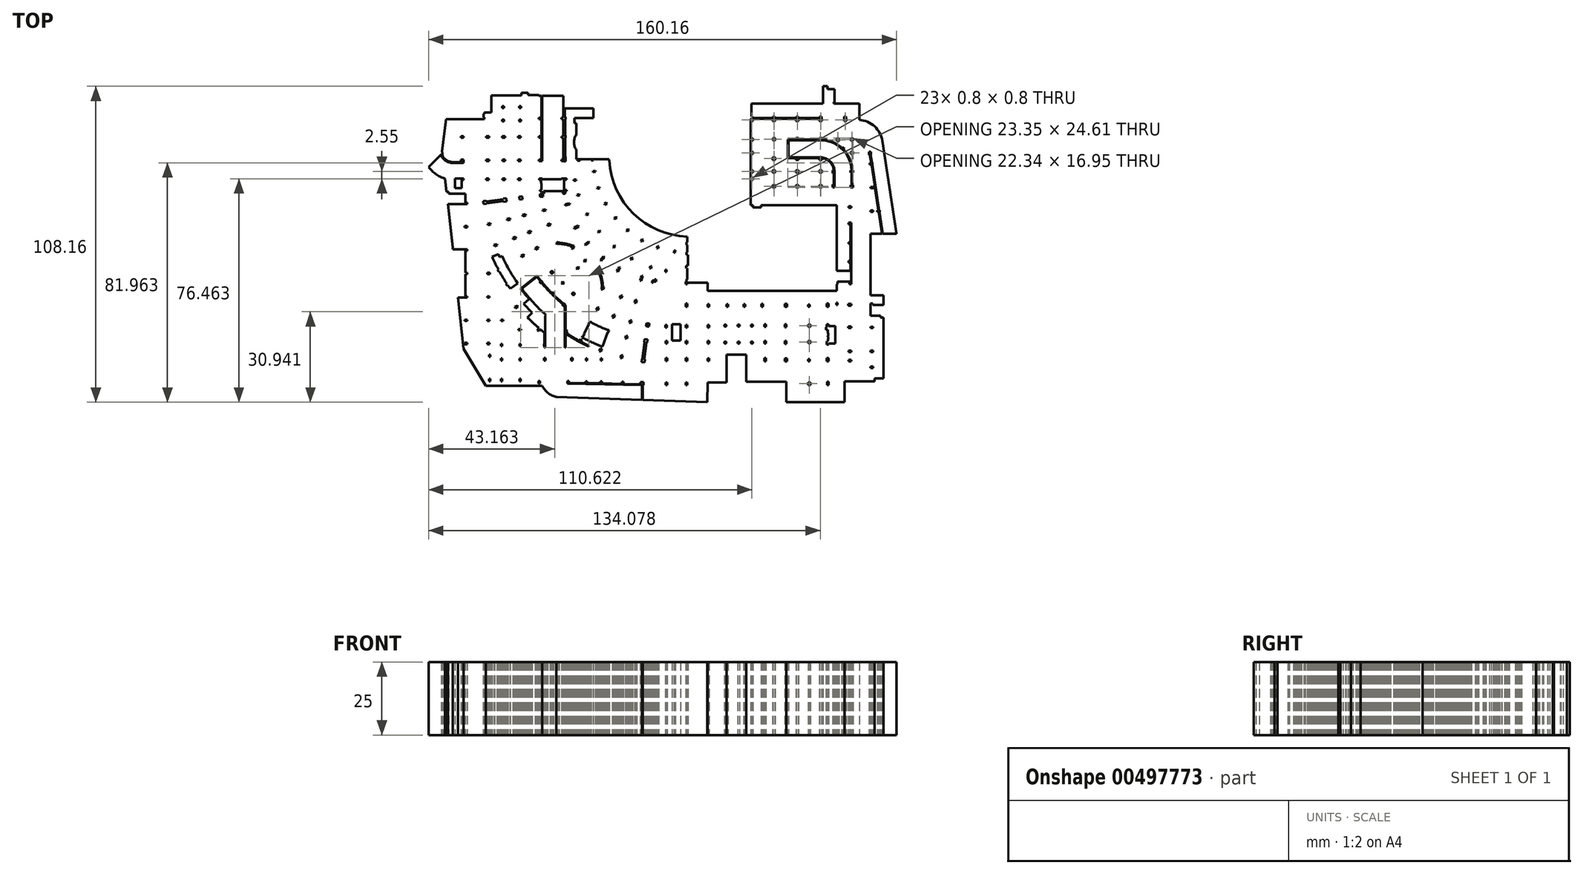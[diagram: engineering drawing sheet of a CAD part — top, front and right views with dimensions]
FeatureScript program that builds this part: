
annotation { "Feature Type Name" : "Feature", "Feature Type Description" : "" }
export const myFeature = defineFeature(function(context is Context, id is Id, definition is map)
    precondition{}
    {
        {
            var Q0;
            Q0=qCreatedBy(makeId("Top.planeOp"),FACE);
            var sketch = newSketch(context, id + "F0", { "sketchPlane" : qUnion([Q0])});
            skLineSegment(sketch, "E0", {"start": v(3.19, -27.44) * mm, "end": v(3.19, -32.96) * mm});
            skLineSegment(sketch, "E1", {"start": v(3.19, -32.96) * mm, "end": v(6.18, -32.96) * mm});
            skLineSegment(sketch, "E2", {"start": v(6.18, -32.96) * mm, "end": v(6.18, -27.44) * mm});
            skLineSegment(sketch, "E3", {"start": v(6.18, -27.44) * mm, "end": v(3.19, -27.44) * mm});
            skLineSegment(sketch, "E4", {"start": v(-41.22, -48.44) * mm, "end": v(-60.5, -48.44) * mm});
            skLineSegment(sketch, "E5", {"start": v(-60.5, -48.44) * mm, "end": v(-68.1, -35.79) * mm});
            skLineSegment(sketch, "E6", {"start": v(-68.1, -35.79) * mm, "end": v(-70, -18.32) * mm});
            skLineSegment(sketch, "E7", {"start": v(-70, -18.32) * mm, "end": v(-66.9, -18.32) * mm});
            skLineSegment(sketch, "E8", {"start": v(-66.9, -18.32) * mm, "end": v(-66.9, -17.92) * mm});
            skLineSegment(sketch, "E9", {"start": v(-66.9, -17.92) * mm, "end": v(-67.46, -17.92) * mm});
            skLineSegment(sketch, "E10", {"start": v(-67.46, -17.92) * mm, "end": v(-67.46, -10.3) * mm});
            skLineSegment(sketch, "E11", {"start": v(-67.46, -10.3) * mm, "end": v(-66.9, -10.3) * mm});
            skLineSegment(sketch, "E12", {"start": v(-66.9, -10.3) * mm, "end": v(-66.9, -9.8) * mm});
            skLineSegment(sketch, "E13", {"start": v(-66.9, -9.8) * mm, "end": v(-67.46, -9.8) * mm});
            skLineSegment(sketch, "E14", {"start": v(-67.46, -9.8) * mm, "end": v(-67.46, -2.3) * mm});
            skLineSegment(sketch, "E15", {"start": v(-67.46, -2.3) * mm, "end": v(-66.9, -2.3) * mm});
            skLineSegment(sketch, "E16", {"start": v(-66.9, -2.3) * mm, "end": v(-66.9, -1.8) * mm});
            skLineSegment(sketch, "E17", {"start": v(-66.9, -1.8) * mm, "end": v(-71.9, -1.8) * mm});
            skLineSegment(sketch, "E18", {"start": v(-71.9, -1.8) * mm, "end": v(-71.88, -1.17) * mm});
            skLineSegment(sketch, "E19", {"start": v(-71.88, -1.17) * mm, "end": v(-73.5, 13.73) * mm});
            skLineSegment(sketch, "E20", {"start": v(-73.5, 13.73) * mm, "end": v(-66.9, 13.73) * mm});
            skLineSegment(sketch, "E21", {"start": v(-66.9, 13.73) * mm, "end": v(-66.9, 14.23) * mm});
            skLineSegment(sketch, "E22", {"start": v(-66.9, 14.23) * mm, "end": v(-67.56, 14.23) * mm});
            skLineSegment(sketch, "E23", {"start": v(-67.56, 14.23) * mm, "end": v(-67.56, 17.23) * mm});
            skLineSegment(sketch, "E24", {"start": v(-67.56, 17.23) * mm, "end": v(-73.17, 17.23) * mm});
            skLineSegment(sketch, "E25", {"start": v(-73.17, 17.23) * mm, "end": v(-73.17, 17.95) * mm});
            skLineSegment(sketch, "E26", {"start": v(-73.17, 17.95) * mm, "end": v(-73.97, 17.95) * mm});
            skLineSegment(sketch, "E27", {"start": v(-73.97, 17.95) * mm, "end": v(-74.47, 22.49) * mm});
            skLineSegment(sketch, "E28", {"start": v(-71.03, 22.46) * mm, "end": v(-68.18, 22.46) * mm});
            skLineSegment(sketch, "E29", {"start": v(-68.18, 22.46) * mm, "end": v(-68.18, 21.96) * mm});
            skLineSegment(sketch, "E30", {"start": v(-68.18, 21.96) * mm, "end": v(-68.83, 21.96) * mm});
            skLineSegment(sketch, "E31", {"start": v(-68.83, 21.96) * mm, "end": v(-68.83, 19.26) * mm});
            skLineSegment(sketch, "E32", {"start": v(-68.83, 19.26) * mm, "end": v(-71.03, 19.26) * mm});
            skLineSegment(sketch, "E33", {"start": v(-71.03, 19.26) * mm, "end": v(-71.03, 22.46) * mm});
            skArc(sketch, "E34", {"start": v(-80.08, 26.47) * mm, "mid": v(-77.61, 24) * mm, "end": v(-74.47, 22.49) * mm});
            skLineSegment(sketch, "E35", {"start": v(-80.08, 26.47) * mm, "end": v(-76.37, 30.18) * mm});
            skLineSegment(sketch, "E36", {"start": v(-76.37, 30.18) * mm, "end": v(-75.78, 30.77) * mm});
            skLineSegment(sketch, "E37", {"start": v(-75.78, 30.77) * mm, "end": v(-75.7, 30.12) * mm});
            skArc(sketch, "E38", {"start": v(-75.7, 30.12) * mm, "mid": v(-73.92, 28.4) * mm, "end": v(-71.51, 27.78) * mm});
            skLineSegment(sketch, "E39", {"start": v(-71.51, 27.78) * mm, "end": v(-68.18, 27.78) * mm});
            skLineSegment(sketch, "E40", {"start": v(-68.18, 27.78) * mm, "end": v(-68.18, 28.98) * mm});
            skLineSegment(sketch, "E41", {"start": v(-68.18, 28.98) * mm, "end": v(-69.08, 28.98) * mm});
            skLineSegment(sketch, "E42", {"start": v(-69.08, 28.98) * mm, "end": v(-69.08, 28.08) * mm});
            skLineSegment(sketch, "E43", {"start": v(-69.08, 28.08) * mm, "end": v(-71.6, 28.08) * mm});
            skArc(sketch, "E44", {"start": v(-75.3, 30.04) * mm, "mid": v(-73.68, 28.6) * mm, "end": v(-71.6, 28.08) * mm});
            skLineSegment(sketch, "E45", {"start": v(-75.3, 30.04) * mm, "end": v(-75.5, 31.91) * mm});
            skLineSegment(sketch, "E46", {"start": v(-75.5, 31.91) * mm, "end": v(-74.07, 42.76) * mm});
            skLineSegment(sketch, "E47", {"start": v(-74.07, 42.76) * mm, "end": v(-60.98, 42.76) * mm});
            skLineSegment(sketch, "E48", {"start": v(-60.98, 42.76) * mm, "end": v(-60.98, 43.46) * mm});
            skLineSegment(sketch, "E49", {"start": v(-60.98, 43.46) * mm, "end": v(-61.28, 43.46) * mm});
            skLineSegment(sketch, "E50", {"start": v(-61.28, 43.46) * mm, "end": v(-61.28, 44.66) * mm});
            skLineSegment(sketch, "E51", {"start": v(-61.28, 44.66) * mm, "end": v(-60.98, 44.66) * mm});
            skLineSegment(sketch, "E52", {"start": v(-60.98, 44.66) * mm, "end": v(-60.98, 45.1) * mm});
            skLineSegment(sketch, "E53", {"start": v(-60.98, 45.1) * mm, "end": v(-58.66, 45.1) * mm});
            skLineSegment(sketch, "E54", {"start": v(-58.66, 45.1) * mm, "end": v(-58.66, 50.96) * mm});
            skLineSegment(sketch, "E55", {"start": v(-58.66, 50.96) * mm, "end": v(-48.31, 50.98) * mm});
            skLineSegment(sketch, "E56", {"start": v(-48.31, 50.98) * mm, "end": v(-48.31, 51.81) * mm});
            skLineSegment(sketch, "E57", {"start": v(-48.31, 51.81) * mm, "end": v(-46.03, 51.81) * mm});
            skLineSegment(sketch, "E58", {"start": v(-46.03, 51.81) * mm, "end": v(-46.03, 51.03) * mm});
            skLineSegment(sketch, "E59", {"start": v(-46.03, 51.03) * mm, "end": v(-42.33, 51.03) * mm});
            skLineSegment(sketch, "E60", {"start": v(-42.33, 51.03) * mm, "end": v(-42.33, 50.78) * mm});
            skLineSegment(sketch, "E61", {"start": v(-42.33, 50.78) * mm, "end": v(-41.48, 50.78) * mm});
            skLineSegment(sketch, "E62", {"start": v(-41.48, 50.78) * mm, "end": v(-41.48, 43.28) * mm});
            skLineSegment(sketch, "E63", {"start": v(-41.48, 43.28) * mm, "end": v(-42.33, 43.28) * mm});
            skLineSegment(sketch, "E64", {"start": v(-42.33, 43.28) * mm, "end": v(-42.33, 42.78) * mm});
            skLineSegment(sketch, "E65", {"start": v(-42.33, 42.78) * mm, "end": v(-41.48, 42.78) * mm});
            skLineSegment(sketch, "E66", {"start": v(-41.48, 42.78) * mm, "end": v(-41.48, 36.98) * mm});
            skLineSegment(sketch, "E67", {"start": v(-41.48, 36.98) * mm, "end": v(-42.33, 36.98) * mm});
            skLineSegment(sketch, "E68", {"start": v(-42.33, 36.98) * mm, "end": v(-42.33, 36.48) * mm});
            skLineSegment(sketch, "E69", {"start": v(-42.33, 36.48) * mm, "end": v(-41.48, 36.48) * mm});
            skLineSegment(sketch, "E70", {"start": v(-41.48, 36.48) * mm, "end": v(-41.48, 28.98) * mm});
            skLineSegment(sketch, "E71", {"start": v(-41.48, 28.98) * mm, "end": v(-42.33, 28.98) * mm});
            skLineSegment(sketch, "E72", {"start": v(-42.33, 28.98) * mm, "end": v(-42.33, 28.48) * mm});
            skLineSegment(sketch, "E73", {"start": v(-42.33, 28.48) * mm, "end": v(-41.23, 28.48) * mm});
            skLineSegment(sketch, "E74", {"start": v(-41.23, 28.48) * mm, "end": v(-41.23, 28.65) * mm});
            skLineSegment(sketch, "E75", {"start": v(-41.23, 28.65) * mm, "end": v(-41.23, 50.78) * mm});
            skLineSegment(sketch, "E76", {"start": v(-41.23, 50.78) * mm, "end": v(-33.98, 50.78) * mm});
            skLineSegment(sketch, "E77", {"start": v(-33.98, 50.78) * mm, "end": v(-33.98, 43.28) * mm});
            skLineSegment(sketch, "E78", {"start": v(-33.98, 43.28) * mm, "end": v(-34.58, 43.28) * mm});
            skLineSegment(sketch, "E79", {"start": v(-34.58, 43.28) * mm, "end": v(-34.58, 42.78) * mm});
            skLineSegment(sketch, "E80", {"start": v(-34.58, 42.78) * mm, "end": v(-33.98, 42.78) * mm});
            skLineSegment(sketch, "E81", {"start": v(-33.98, 42.78) * mm, "end": v(-33.98, 36.9) * mm});
            skLineSegment(sketch, "E82", {"start": v(-33.98, 36.9) * mm, "end": v(-34.58, 36.9) * mm});
            skLineSegment(sketch, "E83", {"start": v(-34.58, 36.9) * mm, "end": v(-34.58, 36.4) * mm});
            skLineSegment(sketch, "E84", {"start": v(-34.58, 36.4) * mm, "end": v(-33.93, 36.4) * mm});
            skLineSegment(sketch, "E85", {"start": v(-33.93, 36.4) * mm, "end": v(-33.93, 28.98) * mm});
            skLineSegment(sketch, "E86", {"start": v(-33.93, 28.98) * mm, "end": v(-34.58, 28.98) * mm});
            skLineSegment(sketch, "E87", {"start": v(-34.58, 28.98) * mm, "end": v(-34.58, 28.48) * mm});
            skLineSegment(sketch, "E88", {"start": v(-34.58, 28.48) * mm, "end": v(-33.63, 28.48) * mm});
            skLineSegment(sketch, "E89", {"start": v(-33.63, 28.48) * mm, "end": v(-33.63, 28.29) * mm});
            skLineSegment(sketch, "E90", {"start": v(-33.63, 28.29) * mm, "end": v(-33.23, 28.29) * mm});
            skLineSegment(sketch, "E91", {"start": v(-33.23, 28.29) * mm, "end": v(-33.23, 29.94) * mm});
            skLineSegment(sketch, "E92", {"start": v(-33.23, 29.94) * mm, "end": v(-33.38, 29.94) * mm});
            skLineSegment(sketch, "E93", {"start": v(-33.38, 29.94) * mm, "end": v(-33.38, 36.4) * mm});
            skLineSegment(sketch, "E94", {"start": v(-33.38, 36.4) * mm, "end": v(-33.23, 36.4) * mm});
            skLineSegment(sketch, "E95", {"start": v(-33.23, 36.4) * mm, "end": v(-33.23, 37.2) * mm});
            skLineSegment(sketch, "E96", {"start": v(-33.23, 37.2) * mm, "end": v(-33.38, 37.2) * mm});
            skLineSegment(sketch, "E97", {"start": v(-33.38, 37.2) * mm, "end": v(-33.38, 42.78) * mm});
            skLineSegment(sketch, "E98", {"start": v(-33.38, 42.78) * mm, "end": v(-33.23, 42.78) * mm});
            skLineSegment(sketch, "E99", {"start": v(-33.23, 42.78) * mm, "end": v(-33.23, 43.58) * mm});
            skLineSegment(sketch, "E100", {"start": v(-33.23, 43.58) * mm, "end": v(-33.51, 43.58) * mm});
            skLineSegment(sketch, "E101", {"start": v(-33.51, 43.58) * mm, "end": v(-33.51, 46.5) * mm});
            skLineSegment(sketch, "E102", {"start": v(-33.51, 46.5) * mm, "end": v(-23.68, 46.5) * mm});
            skLineSegment(sketch, "E103", {"start": v(-23.68, 46.5) * mm, "end": v(-23.68, 43.2) * mm});
            skLineSegment(sketch, "E104", {"start": v(-23.68, 43.2) * mm, "end": v(-30.13, 43.2) * mm});
            skLineSegment(sketch, "E105", {"start": v(-30.13, 43.2) * mm, "end": v(-30.13, 41.39) * mm});
            skLineSegment(sketch, "E106", {"start": v(-30.13, 41.39) * mm, "end": v(-29.51, 41.39) * mm});
            skLineSegment(sketch, "E107", {"start": v(-29.51, 41.39) * mm, "end": v(-29.51, 37.58) * mm});
            skArc(sketch, "E108", {"start": v(-29.51, 37.58) * mm, "mid": v(-30.33, 34.9) * mm, "end": v(-29.51, 32.24) * mm});
            skLineSegment(sketch, "E109", {"start": v(-29.51, 32.24) * mm, "end": v(-29.51, 29.14) * mm});
            skLineSegment(sketch, "E110", {"start": v(-29.51, 29.14) * mm, "end": v(-18.3, 29.09) * mm});
            skLineSegment(sketch, "E111", {"start": v(-18.3, 29.09) * mm, "end": v(-18.3, 28.69) * mm});
            skLineSegment(sketch, "E112", {"start": v(-18.3, 28.69) * mm, "end": v(-18.26, 28.69) * mm});
            skArc(sketch, "E113", {"start": v(-18.26, 28.69) * mm, "mid": v(-9.97, 10.44) * mm, "end": v(8.48, 2.6) * mm});
            skLineSegment(sketch, "E114", {"start": v(8.48, 2.6) * mm, "end": v(8.48, 0.6) * mm});
            skLineSegment(sketch, "E115", {"start": v(8.48, 0.6) * mm, "end": v(8.2, 0.6) * mm});
            skLineSegment(sketch, "E116", {"start": v(8.2, 0.6) * mm, "end": v(8.2, -0.2) * mm});
            skLineSegment(sketch, "E117", {"start": v(8.2, -0.2) * mm, "end": v(8.48, -0.2) * mm});
            skLineSegment(sketch, "E118", {"start": v(8.48, -0.2) * mm, "end": v(8.48, -2.82) * mm});
            skLineSegment(sketch, "E119", {"start": v(8.48, -2.82) * mm, "end": v(8.2, -2.82) * mm});
            skLineSegment(sketch, "E120", {"start": v(8.2, -2.82) * mm, "end": v(8.2, -3.62) * mm});
            skLineSegment(sketch, "E121", {"start": v(8.2, -3.62) * mm, "end": v(8.65, -3.62) * mm});
            skLineSegment(sketch, "E122", {"start": v(8.65, -3.62) * mm, "end": v(8.65, -7.32) * mm});
            skLineSegment(sketch, "E123", {"start": v(8.65, -7.32) * mm, "end": v(8.1, -7.32) * mm});
            skLineSegment(sketch, "E124", {"start": v(8.1, -7.32) * mm, "end": v(8.1, -8.22) * mm});
            skLineSegment(sketch, "E125", {"start": v(8.1, -8.22) * mm, "end": v(8.48, -8.22) * mm});
            skLineSegment(sketch, "E126", {"start": v(8.48, -8.22) * mm, "end": v(8.48, -12) * mm});
            skLineSegment(sketch, "E127", {"start": v(8.48, -12) * mm, "end": v(8.2, -12) * mm});
            skLineSegment(sketch, "E128", {"start": v(8.2, -12) * mm, "end": v(8.2, -12.84) * mm});
            skLineSegment(sketch, "E129", {"start": v(8.2, -12.84) * mm, "end": v(7.96, -12.84) * mm});
            skLineSegment(sketch, "E130", {"start": v(7.96, -12.84) * mm, "end": v(7.96, -13.74) * mm});
            skLineSegment(sketch, "E131", {"start": v(7.96, -13.74) * mm, "end": v(8.46, -13.74) * mm});
            skLineSegment(sketch, "E132", {"start": v(8.46, -13.74) * mm, "end": v(8.46, -13.14) * mm});
            skLineSegment(sketch, "E133", {"start": v(8.46, -13.14) * mm, "end": v(15.42, -13.14) * mm});
            skLineSegment(sketch, "E134", {"start": v(15.42, -13.14) * mm, "end": v(15.42, -15.94) * mm});
            skLineSegment(sketch, "E135", {"start": v(15.42, -15.94) * mm, "end": v(59.59, -15.94) * mm});
            skLineSegment(sketch, "E136", {"start": v(59.59, -15.94) * mm, "end": v(59.59, -13.64) * mm});
            skLineSegment(sketch, "E137", {"start": v(59.59, -13.64) * mm, "end": v(59.87, -13.64) * mm});
            skLineSegment(sketch, "E138", {"start": v(59.87, -13.64) * mm, "end": v(59.87, -12.8) * mm});
            skLineSegment(sketch, "E139", {"start": v(59.87, -12.8) * mm, "end": v(64.62, -12.8) * mm});
            skLineSegment(sketch, "E140", {"start": v(64.62, -12.8) * mm, "end": v(64.62, 7.4) * mm});
            skLineSegment(sketch, "E141", {"start": v(64.62, 7.4) * mm, "end": v(63.62, 7.4) * mm});
            skLineSegment(sketch, "E142", {"start": v(63.62, 7.4) * mm, "end": v(63.62, 6.8) * mm});
            skLineSegment(sketch, "E143", {"start": v(63.62, 6.8) * mm, "end": v(64.37, 6.8) * mm});
            skLineSegment(sketch, "E144", {"start": v(64.37, 6.8) * mm, "end": v(64.37, 0.7) * mm});
            skLineSegment(sketch, "E145", {"start": v(64.37, 0.7) * mm, "end": v(63.62, 0.7) * mm});
            skLineSegment(sketch, "E146", {"start": v(63.62, 0.7) * mm, "end": v(63.62, 0.1) * mm});
            skLineSegment(sketch, "E147", {"start": v(63.62, 0.1) * mm, "end": v(64.37, 0.1) * mm});
            skLineSegment(sketch, "E148", {"start": v(64.37, 0.1) * mm, "end": v(64.37, -5.7) * mm});
            skLineSegment(sketch, "E149", {"start": v(64.37, -5.7) * mm, "end": v(63.62, -5.7) * mm});
            skLineSegment(sketch, "E150", {"start": v(63.62, -5.7) * mm, "end": v(63.62, -6.3) * mm});
            skLineSegment(sketch, "E151", {"start": v(63.62, -6.3) * mm, "end": v(64.37, -6.3) * mm});
            skLineSegment(sketch, "E152", {"start": v(64.37, -6.3) * mm, "end": v(64.37, -9.08) * mm});
            skLineSegment(sketch, "E153", {"start": v(64.37, -9.08) * mm, "end": v(59.59, -9.08) * mm});
            skLineSegment(sketch, "E154", {"start": v(59.59, -9.08) * mm, "end": v(59.59, 13.32) * mm});
            skLineSegment(sketch, "E155", {"start": v(59.59, 13.32) * mm, "end": v(33.72, 13.33) * mm});
            skLineSegment(sketch, "E156", {"start": v(33.72, 13.33) * mm, "end": v(33.72, 12.65) * mm});
            skLineSegment(sketch, "E157", {"start": v(33.72, 12.65) * mm, "end": v(30.94, 12.65) * mm});
            skLineSegment(sketch, "E158", {"start": v(30.94, 12.65) * mm, "end": v(30.94, 13.33) * mm});
            skLineSegment(sketch, "E159", {"start": v(30.94, 13.33) * mm, "end": v(30.1, 13.33) * mm});
            skLineSegment(sketch, "E160", {"start": v(30.1, 13.33) * mm, "end": v(30.1, 43) * mm});
            skLineSegment(sketch, "E161", {"start": v(30.1, 43) * mm, "end": v(54.44, 43) * mm});
            skLineSegment(sketch, "E162", {"start": v(54.44, 43) * mm, "end": v(54.44, 43.7) * mm});
            skLineSegment(sketch, "E163", {"start": v(54.44, 43.7) * mm, "end": v(53.74, 43.7) * mm});
            skLineSegment(sketch, "E164", {"start": v(53.74, 43.7) * mm, "end": v(53.74, 43.26) * mm});
            skLineSegment(sketch, "E165", {"start": v(53.74, 43.26) * mm, "end": v(46.44, 43.26) * mm});
            skLineSegment(sketch, "E166", {"start": v(46.44, 43.26) * mm, "end": v(46.44, 43.7) * mm});
            skLineSegment(sketch, "E167", {"start": v(46.44, 43.7) * mm, "end": v(45.74, 43.7) * mm});
            skLineSegment(sketch, "E168", {"start": v(45.74, 43.7) * mm, "end": v(45.74, 43.26) * mm});
            skLineSegment(sketch, "E169", {"start": v(45.74, 43.26) * mm, "end": v(38.44, 43.26) * mm});
            skLineSegment(sketch, "E170", {"start": v(38.44, 43.26) * mm, "end": v(38.44, 43.7) * mm});
            skLineSegment(sketch, "E171", {"start": v(38.44, 43.7) * mm, "end": v(37.74, 43.7) * mm});
            skLineSegment(sketch, "E172", {"start": v(37.74, 43.7) * mm, "end": v(37.74, 43.26) * mm});
            skLineSegment(sketch, "E173", {"start": v(37.74, 43.26) * mm, "end": v(30.84, 43.26) * mm});
            skLineSegment(sketch, "E174", {"start": v(30.84, 43.26) * mm, "end": v(30.84, 43.7) * mm});
            skLineSegment(sketch, "E175", {"start": v(30.84, 43.7) * mm, "end": v(30.4, 43.7) * mm});
            skLineSegment(sketch, "E176", {"start": v(30.4, 43.7) * mm, "end": v(30.4, 48.19) * mm});
            skLineSegment(sketch, "E177", {"start": v(30.4, 48.19) * mm, "end": v(54.9, 48.19) * mm});
            skLineSegment(sketch, "E178", {"start": v(54.9, 48.19) * mm, "end": v(54.9, 54.08) * mm});
            skLineSegment(sketch, "E179", {"start": v(54.9, 54.08) * mm, "end": v(56.5, 54.08) * mm});
            skLineSegment(sketch, "E180", {"start": v(56.5, 54.08) * mm, "end": v(56.5, 53.08) * mm});
            skLineSegment(sketch, "E181", {"start": v(56.5, 53.08) * mm, "end": v(58.8, 53.08) * mm});
            skLineSegment(sketch, "E182", {"start": v(58.8, 53.08) * mm, "end": v(58.8, 48.68) * mm});
            skLineSegment(sketch, "E183", {"start": v(58.8, 48.68) * mm, "end": v(58.6, 48.68) * mm});
            skLineSegment(sketch, "E184", {"start": v(58.6, 48.68) * mm, "end": v(58.6, 48.18) * mm});
            skLineSegment(sketch, "E185", {"start": v(58.6, 48.18) * mm, "end": v(67.35, 48.18) * mm});
            skLineSegment(sketch, "E186", {"start": v(67.35, 48.18) * mm, "end": v(67.37, 48.18) * mm});
            skLineSegment(sketch, "E187", {"start": v(67.37, 48.18) * mm, "end": v(67.37, 42.54) * mm});
            skArc(sketch, "E188", {"start": v(75.2, 35.39) * mm, "mid": v(72.55, 40.35) * mm, "end": v(67.37, 42.54) * mm});
            skLineSegment(sketch, "E189", {"start": v(75.2, 35.39) * mm, "end": v(80.08, 3.6) * mm});
            skLineSegment(sketch, "E190", {"start": v(80.08, 3.6) * mm, "end": v(75.37, 3.6) * mm});
            skLineSegment(sketch, "E191", {"start": v(75.37, 3.6) * mm, "end": v(74.22, 11.1) * mm});
            skLineSegment(sketch, "E192", {"start": v(74.22, 11.1) * mm, "end": v(74.33, 11.1) * mm});
            skLineSegment(sketch, "E193", {"start": v(74.33, 11.1) * mm, "end": v(74.33, 11.6) * mm});
            skLineSegment(sketch, "E194", {"start": v(74.33, 11.6) * mm, "end": v(74.15, 11.6) * mm});
            skLineSegment(sketch, "E195", {"start": v(74.15, 11.6) * mm, "end": v(71.75, 27.2) * mm});
            skLineSegment(sketch, "E196", {"start": v(71.75, 27.2) * mm, "end": v(71.86, 27.2) * mm});
            skLineSegment(sketch, "E197", {"start": v(71.86, 27.2) * mm, "end": v(71.86, 27.8) * mm});
            skLineSegment(sketch, "E198", {"start": v(71.86, 27.8) * mm, "end": v(71.66, 27.8) * mm});
            skLineSegment(sketch, "E199", {"start": v(71.66, 27.8) * mm, "end": v(71.22, 30.68) * mm});
            skLineSegment(sketch, "E200", {"start": v(71.22, 30.68) * mm, "end": v(71.3, 30.68) * mm});
            skLineSegment(sketch, "E201", {"start": v(71.3, 30.68) * mm, "end": v(71.3, 31.68) * mm});
            skLineSegment(sketch, "E202", {"start": v(71.3, 31.68) * mm, "end": v(70.7, 31.68) * mm});
            skLineSegment(sketch, "E203", {"start": v(70.7, 31.68) * mm, "end": v(70.7, 30.68) * mm});
            skLineSegment(sketch, "E204", {"start": v(70.7, 30.68) * mm, "end": v(70.97, 30.68) * mm});
            skLineSegment(sketch, "E205", {"start": v(70.97, 30.68) * mm, "end": v(71.4, 27.8) * mm});
            skLineSegment(sketch, "E206", {"start": v(71.4, 27.8) * mm, "end": v(70.86, 27.8) * mm});
            skLineSegment(sketch, "E207", {"start": v(70.86, 27.8) * mm, "end": v(70.86, 27.2) * mm});
            skLineSegment(sketch, "E208", {"start": v(70.86, 27.2) * mm, "end": v(71.5, 27.2) * mm});
            skLineSegment(sketch, "E209", {"start": v(71.5, 27.2) * mm, "end": v(72.67, 19.6) * mm});
            skLineSegment(sketch, "E210", {"start": v(72.67, 19.6) * mm, "end": v(71.17, 19.6) * mm});
            skLineSegment(sketch, "E211", {"start": v(71.17, 19.6) * mm, "end": v(71.17, 19.2) * mm});
            skLineSegment(sketch, "E212", {"start": v(71.17, 19.2) * mm, "end": v(72.73, 19.2) * mm});
            skLineSegment(sketch, "E213", {"start": v(72.73, 19.2) * mm, "end": v(73.9, 11.6) * mm});
            skLineSegment(sketch, "E214", {"start": v(73.9, 11.6) * mm, "end": v(73.43, 11.6) * mm});
            skLineSegment(sketch, "E215", {"start": v(73.43, 11.6) * mm, "end": v(73.43, 11.1) * mm});
            skLineSegment(sketch, "E216", {"start": v(73.43, 11.1) * mm, "end": v(73.97, 11.1) * mm});
            skLineSegment(sketch, "E217", {"start": v(73.97, 11.1) * mm, "end": v(75.12, 3.6) * mm});
            skLineSegment(sketch, "E218", {"start": v(75.12, 3.6) * mm, "end": v(71.17, 3.6) * mm});
            skLineSegment(sketch, "E219", {"start": v(71.17, 3.6) * mm, "end": v(71.17, -17.5) * mm});
            skLineSegment(sketch, "E220", {"start": v(71.17, -17.5) * mm, "end": v(75.66, -17.5) * mm});
            skLineSegment(sketch, "E221", {"start": v(75.66, -17.5) * mm, "end": v(75.66, -20.8) * mm});
            skLineSegment(sketch, "E222", {"start": v(75.66, -20.8) * mm, "end": v(71.97, -20.8) * mm});
            skLineSegment(sketch, "E223", {"start": v(71.97, -20.8) * mm, "end": v(71.97, -20.24) * mm});
            skLineSegment(sketch, "E224", {"start": v(71.97, -20.24) * mm, "end": v(71.17, -20.24) * mm});
            skLineSegment(sketch, "E225", {"start": v(71.17, -20.24) * mm, "end": v(71.17, -24.46) * mm});
            skLineSegment(sketch, "E226", {"start": v(71.17, -24.46) * mm, "end": v(74.64, -24.46) * mm});
            skLineSegment(sketch, "E227", {"start": v(74.64, -24.46) * mm, "end": v(74.64, -25.18) * mm});
            skLineSegment(sketch, "E228", {"start": v(74.64, -25.18) * mm, "end": v(75.66, -25.18) * mm});
            skLineSegment(sketch, "E229", {"start": v(75.66, -25.18) * mm, "end": v(75.66, -46) * mm});
            skLineSegment(sketch, "E230", {"start": v(75.66, -46) * mm, "end": v(72.54, -46) * mm});
            skLineSegment(sketch, "E231", {"start": v(72.54, -46) * mm, "end": v(72.54, -47.02) * mm});
            skLineSegment(sketch, "E232", {"start": v(72.54, -47.02) * mm, "end": v(62.34, -47.02) * mm});
            skLineSegment(sketch, "E233", {"start": v(62.34, -47.02) * mm, "end": v(62.34, -54.08) * mm});
            skLineSegment(sketch, "E234", {"start": v(62.34, -54.08) * mm, "end": v(42.34, -54.08) * mm});
            skLineSegment(sketch, "E235", {"start": v(42.34, -54.08) * mm, "end": v(42.34, -47.1) * mm});
            skLineSegment(sketch, "E236", {"start": v(42.34, -47.1) * mm, "end": v(28.57, -47.1) * mm});
            skLineSegment(sketch, "E237", {"start": v(28.57, -47.1) * mm, "end": v(28.57, -37.77) * mm});
            skLineSegment(sketch, "E238", {"start": v(28.57, -37.77) * mm, "end": v(21.87, -37.77) * mm});
            skLineSegment(sketch, "E239", {"start": v(21.87, -37.77) * mm, "end": v(21.87, -47.3) * mm});
            skLineSegment(sketch, "E240", {"start": v(21.87, -47.3) * mm, "end": v(15.42, -47.3) * mm});
            skLineSegment(sketch, "E241", {"start": v(15.42, -47.3) * mm, "end": v(15.23, -54.08) * mm});
            skLineSegment(sketch, "E242", {"start": v(15.23, -54.08) * mm, "end": v(-6.8, -53.3) * mm});
            skLineSegment(sketch, "E243", {"start": v(-6.8, -53.3) * mm, "end": v(-6.8, -48.2) * mm});
            skLineSegment(sketch, "E244", {"start": v(-6.8, -48.2) * mm, "end": v(-6.56, -48.2) * mm});
            skLineSegment(sketch, "E245", {"start": v(-6.56, -48.2) * mm, "end": v(-6.56, -47.2) * mm});
            skLineSegment(sketch, "E246", {"start": v(-6.56, -47.2) * mm, "end": v(-7.6, -47.2) * mm});
            skLineSegment(sketch, "E247", {"start": v(-7.6, -47.2) * mm, "end": v(-7.6, -47.93) * mm});
            skLineSegment(sketch, "E248", {"start": v(-7.6, -47.93) * mm, "end": v(-13.46, -47.81) * mm});
            skLineSegment(sketch, "E249", {"start": v(-13.46, -47.81) * mm, "end": v(-13.46, -47.16) * mm});
            skLineSegment(sketch, "E250", {"start": v(-13.46, -47.16) * mm, "end": v(-13.96, -47.16) * mm});
            skLineSegment(sketch, "E251", {"start": v(-13.96, -47.16) * mm, "end": v(-13.96, -47.8) * mm});
            skLineSegment(sketch, "E252", {"start": v(-13.96, -47.8) * mm, "end": v(-20.76, -47.67) * mm});
            skLineSegment(sketch, "E253", {"start": v(-20.76, -47.67) * mm, "end": v(-20.76, -47.01) * mm});
            skLineSegment(sketch, "E254", {"start": v(-20.76, -47.01) * mm, "end": v(-21.26, -47.01) * mm});
            skLineSegment(sketch, "E255", {"start": v(-21.26, -47.01) * mm, "end": v(-21.26, -47.66) * mm});
            skLineSegment(sketch, "E256", {"start": v(-21.26, -47.66) * mm, "end": v(-25.8, -47.57) * mm});
            skLineSegment(sketch, "E257", {"start": v(-25.8, -47.57) * mm, "end": v(-25.8, -46.92) * mm});
            skLineSegment(sketch, "E258", {"start": v(-25.8, -46.92) * mm, "end": v(-26.3, -46.92) * mm});
            skLineSegment(sketch, "E259", {"start": v(-26.3, -46.92) * mm, "end": v(-26.3, -47.56) * mm});
            skLineSegment(sketch, "E260", {"start": v(-26.3, -47.56) * mm, "end": v(-32.08, -47.44) * mm});
            skLineSegment(sketch, "E261", {"start": v(-32.08, -47.44) * mm, "end": v(-32.08, -46.8) * mm});
            skLineSegment(sketch, "E262", {"start": v(-32.08, -46.8) * mm, "end": v(-32.58, -46.8) * mm});
            skLineSegment(sketch, "E263", {"start": v(-32.58, -46.8) * mm, "end": v(-32.58, -47.7) * mm});
            skLineSegment(sketch, "E264", {"start": v(-32.58, -47.7) * mm, "end": v(-7.06, -48.2) * mm});
            skLineSegment(sketch, "E265", {"start": v(-7.06, -48.2) * mm, "end": v(-7.06, -53.29) * mm});
            skLineSegment(sketch, "E266", {"start": v(-7.06, -53.29) * mm, "end": v(-36.42, -52.25) * mm});
            skArc(sketch, "E267", {"start": v(-41.22, -48.44) * mm, "mid": v(-39.28, -50.93) * mm, "end": v(-36.42, -52.25) * mm});
            skLineSegment(sketch, "E268", {"start": v(-54.88, 36.48) * mm, "end": v(-54.88, 36.98) * mm});
            skLineSegment(sketch, "E269", {"start": v(-54.88, 36.98) * mm, "end": v(-53.98, 36.98) * mm});
            skLineSegment(sketch, "E270", {"start": v(-53.98, 36.98) * mm, "end": v(-53.98, 36.48) * mm});
            skLineSegment(sketch, "E271", {"start": v(-53.98, 36.48) * mm, "end": v(-54.88, 36.48) * mm});
            skLineSegment(sketch, "E272", {"start": v(-69.08, 36.98) * mm, "end": v(-69.08, 36.48) * mm});
            skLineSegment(sketch, "E273", {"start": v(-69.08, 36.48) * mm, "end": v(-68.18, 36.48) * mm});
            skLineSegment(sketch, "E274", {"start": v(-68.18, 36.48) * mm, "end": v(-68.18, 36.98) * mm});
            skLineSegment(sketch, "E275", {"start": v(-68.18, 36.98) * mm, "end": v(-69.08, 36.98) * mm});
            skLineSegment(sketch, "E276", {"start": v(-54.88, 47.2) * mm, "end": v(-54.88, 46.6) * mm});
            skLineSegment(sketch, "E277", {"start": v(-54.88, 46.6) * mm, "end": v(-54.28, 46.6) * mm});
            skLineSegment(sketch, "E278", {"start": v(-54.28, 46.6) * mm, "end": v(-54.28, 47.2) * mm});
            skLineSegment(sketch, "E279", {"start": v(-54.28, 47.2) * mm, "end": v(-54.88, 47.2) * mm});
            skLineSegment(sketch, "E280", {"start": v(-49.08, 47.2) * mm, "end": v(-49.08, 46.6) * mm});
            skLineSegment(sketch, "E281", {"start": v(-49.08, 46.6) * mm, "end": v(-48.48, 46.6) * mm});
            skLineSegment(sketch, "E282", {"start": v(-48.48, 46.6) * mm, "end": v(-48.48, 47.2) * mm});
            skLineSegment(sketch, "E283", {"start": v(-48.48, 47.2) * mm, "end": v(-49.08, 47.2) * mm});
            skCircle(sketch, "E284", {"center": v(-54.58, 42.35) * mm, "radius": 0.35 * mm});
            skCircle(sketch, "E285", {"center": v(-48.78, 42.35) * mm, "radius": 0.35 * mm});
            skLineSegment(sketch, "E286", {"start": v(-60.43, 36.98) * mm, "end": v(-60.43, 36.48) * mm});
            skLineSegment(sketch, "E287", {"start": v(-60.43, 36.48) * mm, "end": v(-59.43, 36.48) * mm});
            skLineSegment(sketch, "E288", {"start": v(-59.43, 36.48) * mm, "end": v(-59.43, 36.98) * mm});
            skLineSegment(sketch, "E289", {"start": v(-59.43, 36.98) * mm, "end": v(-60.43, 36.98) * mm});
            skLineSegment(sketch, "E290", {"start": v(-49.43, 36.98) * mm, "end": v(-49.43, 36.48) * mm});
            skLineSegment(sketch, "E291", {"start": v(-49.43, 36.48) * mm, "end": v(-48.53, 36.48) * mm});
            skLineSegment(sketch, "E292", {"start": v(-48.53, 36.48) * mm, "end": v(-48.53, 36.98) * mm});
            skLineSegment(sketch, "E293", {"start": v(-48.53, 36.98) * mm, "end": v(-49.43, 36.98) * mm});
            skLineSegment(sketch, "E294", {"start": v(-60.43, 28.98) * mm, "end": v(-60.43, 28.48) * mm});
            skLineSegment(sketch, "E295", {"start": v(-60.43, 28.48) * mm, "end": v(-59.33, 28.48) * mm});
            skLineSegment(sketch, "E296", {"start": v(-59.33, 28.48) * mm, "end": v(-59.33, 28.98) * mm});
            skLineSegment(sketch, "E297", {"start": v(-59.33, 28.98) * mm, "end": v(-60.43, 28.98) * mm});
            skLineSegment(sketch, "E298", {"start": v(-54.83, 28.98) * mm, "end": v(-54.83, 28.48) * mm});
            skLineSegment(sketch, "E299", {"start": v(-54.83, 28.48) * mm, "end": v(-53.93, 28.48) * mm});
            skLineSegment(sketch, "E300", {"start": v(-53.93, 28.48) * mm, "end": v(-53.93, 28.98) * mm});
            skLineSegment(sketch, "E301", {"start": v(-53.93, 28.98) * mm, "end": v(-54.83, 28.98) * mm});
            skLineSegment(sketch, "E302", {"start": v(-49.43, 28.48) * mm, "end": v(-49.43, 28.98) * mm});
            skLineSegment(sketch, "E303", {"start": v(-49.43, 28.98) * mm, "end": v(-48.53, 28.98) * mm});
            skLineSegment(sketch, "E304", {"start": v(-48.53, 28.98) * mm, "end": v(-48.53, 28.48) * mm});
            skLineSegment(sketch, "E305", {"start": v(-48.53, 28.48) * mm, "end": v(-49.43, 28.48) * mm});
            skLineSegment(sketch, "E306", {"start": v(-60.43, 22.46) * mm, "end": v(-60.43, 21.96) * mm});
            skLineSegment(sketch, "E307", {"start": v(-60.43, 21.96) * mm, "end": v(-59.53, 21.96) * mm});
            skLineSegment(sketch, "E308", {"start": v(-59.53, 21.96) * mm, "end": v(-59.53, 22.46) * mm});
            skLineSegment(sketch, "E309", {"start": v(-59.53, 22.46) * mm, "end": v(-60.43, 22.46) * mm});
            skLineSegment(sketch, "E310", {"start": v(-54.83, 22.46) * mm, "end": v(-54.83, 21.96) * mm});
            skLineSegment(sketch, "E311", {"start": v(-54.83, 21.96) * mm, "end": v(-53.93, 21.96) * mm});
            skLineSegment(sketch, "E312", {"start": v(-53.93, 21.96) * mm, "end": v(-53.93, 22.46) * mm});
            skLineSegment(sketch, "E313", {"start": v(-53.93, 22.46) * mm, "end": v(-54.83, 22.46) * mm});
            skLineSegment(sketch, "E314", {"start": v(-49.43, 22.46) * mm, "end": v(-49.43, 21.96) * mm});
            skLineSegment(sketch, "E315", {"start": v(-49.43, 21.96) * mm, "end": v(-48.53, 21.96) * mm});
            skLineSegment(sketch, "E316", {"start": v(-48.53, 21.96) * mm, "end": v(-48.53, 22.46) * mm});
            skLineSegment(sketch, "E317", {"start": v(-48.53, 22.46) * mm, "end": v(-49.43, 22.46) * mm});
            skLineSegment(sketch, "E318", {"start": v(-61.37, 14.72) * mm, "end": v(-60.37, 14.85) * mm});
            skLineSegment(sketch, "E319", {"start": v(-60.37, 14.85) * mm, "end": v(-60.35, 14.65) * mm});
            skLineSegment(sketch, "E320", {"start": v(-60.35, 14.65) * mm, "end": v(-54.53, 15.4) * mm});
            skLineSegment(sketch, "E321", {"start": v(-54.53, 15.4) * mm, "end": v(-54.55, 15.6) * mm});
            skLineSegment(sketch, "E322", {"start": v(-54.55, 15.6) * mm, "end": v(-53.56, 15.72) * mm});
            skLineSegment(sketch, "E323", {"start": v(-53.56, 15.72) * mm, "end": v(-53.43, 14.68) * mm});
            skLineSegment(sketch, "E324", {"start": v(-53.43, 14.68) * mm, "end": v(-54.42, 14.55) * mm});
            skLineSegment(sketch, "E325", {"start": v(-54.42, 14.55) * mm, "end": v(-54.44, 14.75) * mm});
            skLineSegment(sketch, "E326", {"start": v(-54.44, 14.75) * mm, "end": v(-60.27, 14) * mm});
            skLineSegment(sketch, "E327", {"start": v(-60.27, 14) * mm, "end": v(-60.24, 13.8) * mm});
            skLineSegment(sketch, "E328", {"start": v(-60.24, 13.8) * mm, "end": v(-61.23, 13.68) * mm});
            skLineSegment(sketch, "E329", {"start": v(-61.23, 13.68) * mm, "end": v(-61.37, 14.72) * mm});
            skLineSegment(sketch, "E330", {"start": v(-49.09, 16.3) * mm, "end": v(-48.96, 15.25) * mm});
            skLineSegment(sketch, "E331", {"start": v(-48.96, 15.25) * mm, "end": v(-47.96, 15.38) * mm});
            skLineSegment(sketch, "E332", {"start": v(-47.96, 15.38) * mm, "end": v(-48.1, 16.42) * mm});
            skLineSegment(sketch, "E333", {"start": v(-48.1, 16.42) * mm, "end": v(-49.09, 16.3) * mm});
            skLineSegment(sketch, "E334", {"start": v(-59.94, 6.97) * mm, "end": v(-58.97, 7.22) * mm});
            skLineSegment(sketch, "E335", {"start": v(-58.97, 7.22) * mm, "end": v(-58.85, 6.73) * mm});
            skLineSegment(sketch, "E336", {"start": v(-58.85, 6.73) * mm, "end": v(-59.82, 6.49) * mm});
            skLineSegment(sketch, "E337", {"start": v(-59.82, 6.49) * mm, "end": v(-59.94, 6.97) * mm});
            skLineSegment(sketch, "E338", {"start": v(-53.28, 8.66) * mm, "end": v(-53.16, 8.18) * mm});
            skLineSegment(sketch, "E339", {"start": v(-53.16, 8.18) * mm, "end": v(-52.19, 8.42) * mm});
            skLineSegment(sketch, "E340", {"start": v(-52.19, 8.42) * mm, "end": v(-52.3, 8.9) * mm});
            skLineSegment(sketch, "E341", {"start": v(-52.3, 8.9) * mm, "end": v(-53.28, 8.66) * mm});
            skLineSegment(sketch, "E342", {"start": v(-47.95, 10) * mm, "end": v(-46.98, 10.25) * mm});
            skLineSegment(sketch, "E343", {"start": v(-46.98, 10.25) * mm, "end": v(-46.85, 9.77) * mm});
            skLineSegment(sketch, "E344", {"start": v(-46.85, 9.77) * mm, "end": v(-47.82, 9.52) * mm});
            skLineSegment(sketch, "E345", {"start": v(-47.82, 9.52) * mm, "end": v(-47.95, 10) * mm});
            skLineSegment(sketch, "E346", {"start": v(-67.8, 6.2) * mm, "end": v(-66.9, 6.2) * mm});
            skLineSegment(sketch, "E347", {"start": v(-66.9, 6.2) * mm, "end": v(-66.9, 5.7) * mm});
            skLineSegment(sketch, "E348", {"start": v(-66.9, 5.7) * mm, "end": v(-67.8, 5.7) * mm});
            skLineSegment(sketch, "E349", {"start": v(-67.8, 5.7) * mm, "end": v(-67.8, 6.2) * mm});
            skLineSegment(sketch, "E350", {"start": v(-57.67, -0.28) * mm, "end": v(-56.73, 0.08) * mm});
            skLineSegment(sketch, "E351", {"start": v(-56.73, 0.08) * mm, "end": v(-56.55, -0.39) * mm});
            skLineSegment(sketch, "E352", {"start": v(-56.55, -0.39) * mm, "end": v(-57.49, -0.75) * mm});
            skLineSegment(sketch, "E353", {"start": v(-57.49, -0.75) * mm, "end": v(-57.67, -0.28) * mm});
            skLineSegment(sketch, "E354", {"start": v(-51.25, 2.2) * mm, "end": v(-50.32, 2.56) * mm});
            skLineSegment(sketch, "E355", {"start": v(-50.32, 2.56) * mm, "end": v(-50.14, 2.09) * mm});
            skLineSegment(sketch, "E356", {"start": v(-50.14, 2.09) * mm, "end": v(-51.07, 1.73) * mm});
            skLineSegment(sketch, "E357", {"start": v(-51.07, 1.73) * mm, "end": v(-51.25, 2.2) * mm});
            skLineSegment(sketch, "E358", {"start": v(-46.12, 4.18) * mm, "end": v(-45.19, 4.54) * mm});
            skLineSegment(sketch, "E359", {"start": v(-45.19, 4.54) * mm, "end": v(-45, 4.07) * mm});
            skLineSegment(sketch, "E360", {"start": v(-45, 4.07) * mm, "end": v(-45.94, 3.7) * mm});
            skLineSegment(sketch, "E361", {"start": v(-45.94, 3.7) * mm, "end": v(-46.12, 4.18) * mm});
            skLineSegment(sketch, "E362", {"start": v(-48.47, -3.98) * mm, "end": v(-47.58, -3.5) * mm});
            skLineSegment(sketch, "E363", {"start": v(-47.58, -3.5) * mm, "end": v(-47.35, -3.95) * mm});
            skLineSegment(sketch, "E364", {"start": v(-47.35, -3.95) * mm, "end": v(-48.23, -4.42) * mm});
            skLineSegment(sketch, "E365", {"start": v(-48.23, -4.42) * mm, "end": v(-48.47, -3.98) * mm});
            skLineSegment(sketch, "E366", {"start": v(-43.61, -1.4) * mm, "end": v(-42.73, -0.93) * mm});
            skLineSegment(sketch, "E367", {"start": v(-42.73, -0.93) * mm, "end": v(-42.5, -1.37) * mm});
            skLineSegment(sketch, "E368", {"start": v(-42.5, -1.37) * mm, "end": v(-43.38, -1.84) * mm});
            skLineSegment(sketch, "E369", {"start": v(-43.38, -1.84) * mm, "end": v(-43.61, -1.4) * mm});
            skLineSegment(sketch, "E370", {"start": v(-60, -9.8) * mm, "end": v(-59.1, -9.8) * mm});
            skLineSegment(sketch, "E371", {"start": v(-59.1, -9.8) * mm, "end": v(-59.1, -10.3) * mm});
            skLineSegment(sketch, "E372", {"start": v(-59.1, -10.3) * mm, "end": v(-60, -10.3) * mm});
            skLineSegment(sketch, "E373", {"start": v(-60, -10.3) * mm, "end": v(-60, -9.8) * mm});
            skLineSegment(sketch, "E374", {"start": v(-54.98, -4.06) * mm, "end": v(-55.78, -4.43) * mm});
            skLineSegment(sketch, "E375", {"start": v(-55.78, -4.43) * mm, "end": v(-56.27, -3.35) * mm});
            skLineSegment(sketch, "E376", {"start": v(-56.27, -3.35) * mm, "end": v(-58.34, -4.33) * mm});
            skArc(sketch, "E377", {"start": v(-58.34, -4.33) * mm, "mid": v(-57.32, -6.51) * mm, "end": v(-56.23, -8.65) * mm});
            skLineSegment(sketch, "E378", {"start": v(-56.23, -8.65) * mm, "end": v(-56.47, -8.78) * mm});
            skLineSegment(sketch, "E379", {"start": v(-56.47, -8.78) * mm, "end": v(-56.1, -9.48) * mm});
            skLineSegment(sketch, "E380", {"start": v(-56.1, -9.48) * mm, "end": v(-55.85, -9.35) * mm});
            skArc(sketch, "E381", {"start": v(-55.85, -9.35) * mm, "mid": v(-54.67, -11.4) * mm, "end": v(-53.41, -13.4) * mm});
            skLineSegment(sketch, "E382", {"start": v(-53.41, -13.4) * mm, "end": v(-53.65, -13.56) * mm});
            skLineSegment(sketch, "E383", {"start": v(-53.65, -13.56) * mm, "end": v(-53.2, -14.22) * mm});
            skLineSegment(sketch, "E384", {"start": v(-53.2, -14.22) * mm, "end": v(-52.97, -14.07) * mm});
            skLineSegment(sketch, "E385", {"start": v(-52.97, -14.07) * mm, "end": v(-52.87, -14.23) * mm});
            skLineSegment(sketch, "E386", {"start": v(-52.87, -14.23) * mm, "end": v(-52.16, -15.25) * mm});
            skLineSegment(sketch, "E387", {"start": v(-52.16, -15.25) * mm, "end": v(-49.57, -13.42) * mm});
            skLineSegment(sketch, "E388", {"start": v(-49.57, -13.42) * mm, "end": v(-50.27, -12.4) * mm});
            skArc(sketch, "E389", {"start": v(-54.98, -4.06) * mm, "mid": v(-52.79, -8.32) * mm, "end": v(-50.27, -12.4) * mm});
            skLineSegment(sketch, "E390", {"start": v(-50.62, -21.47) * mm, "end": v(-49.71, -21.04) * mm});
            skLineSegment(sketch, "E391", {"start": v(-49.71, -21.04) * mm, "end": v(-49.5, -21.5) * mm});
            skLineSegment(sketch, "E392", {"start": v(-49.5, -21.5) * mm, "end": v(-50.4, -21.92) * mm});
            skLineSegment(sketch, "E393", {"start": v(-50.4, -21.92) * mm, "end": v(-50.62, -21.47) * mm});
            skLineSegment(sketch, "E394", {"start": v(-60, -17.92) * mm, "end": v(-59.2, -17.92) * mm});
            skLineSegment(sketch, "E395", {"start": v(-59.2, -17.92) * mm, "end": v(-59.2, -18.32) * mm});
            skLineSegment(sketch, "E396", {"start": v(-59.2, -18.32) * mm, "end": v(-60, -18.32) * mm});
            skLineSegment(sketch, "E397", {"start": v(-60, -18.32) * mm, "end": v(-60, -17.92) * mm});
            skLineSegment(sketch, "E398", {"start": v(-67.7, -25.87) * mm, "end": v(-66.9, -25.87) * mm});
            skLineSegment(sketch, "E399", {"start": v(-66.9, -25.87) * mm, "end": v(-66.9, -26.27) * mm});
            skLineSegment(sketch, "E400", {"start": v(-66.9, -26.27) * mm, "end": v(-67.7, -26.27) * mm});
            skLineSegment(sketch, "E401", {"start": v(-67.7, -26.27) * mm, "end": v(-67.7, -25.87) * mm});
            skLineSegment(sketch, "E402", {"start": v(-60, -25.87) * mm, "end": v(-60, -26.27) * mm});
            skLineSegment(sketch, "E403", {"start": v(-60, -26.27) * mm, "end": v(-59.2, -26.27) * mm});
            skLineSegment(sketch, "E404", {"start": v(-59.2, -26.27) * mm, "end": v(-59.2, -25.87) * mm});
            skLineSegment(sketch, "E405", {"start": v(-59.2, -25.87) * mm, "end": v(-60, -25.87) * mm});
            skLineSegment(sketch, "E406", {"start": v(-55.36, -25.87) * mm, "end": v(-54.56, -25.87) * mm});
            skLineSegment(sketch, "E407", {"start": v(-54.56, -25.87) * mm, "end": v(-54.56, -26.27) * mm});
            skLineSegment(sketch, "E408", {"start": v(-54.56, -26.27) * mm, "end": v(-55.36, -26.27) * mm});
            skLineSegment(sketch, "E409", {"start": v(-55.36, -26.27) * mm, "end": v(-55.36, -25.87) * mm});
            skLineSegment(sketch, "E410", {"start": v(-67.7, -33.82) * mm, "end": v(-66.9, -33.82) * mm});
            skLineSegment(sketch, "E411", {"start": v(-66.9, -33.82) * mm, "end": v(-66.9, -34.22) * mm});
            skLineSegment(sketch, "E412", {"start": v(-66.9, -34.22) * mm, "end": v(-67.7, -34.22) * mm});
            skLineSegment(sketch, "E413", {"start": v(-67.7, -34.22) * mm, "end": v(-67.7, -33.82) * mm});
            skLineSegment(sketch, "E414", {"start": v(-59.4, -46.92) * mm, "end": v(-59.4, -46.12) * mm});
            skLineSegment(sketch, "E415", {"start": v(-59.4, -46.12) * mm, "end": v(-59, -46.12) * mm});
            skLineSegment(sketch, "E416", {"start": v(-59, -46.12) * mm, "end": v(-59, -46.92) * mm});
            skLineSegment(sketch, "E417", {"start": v(-59, -46.92) * mm, "end": v(-59.4, -46.92) * mm});
            skLineSegment(sketch, "E418", {"start": v(-55.3, -46.92) * mm, "end": v(-55.3, -46.12) * mm});
            skLineSegment(sketch, "E419", {"start": v(-55.3, -46.12) * mm, "end": v(-54.9, -46.12) * mm});
            skLineSegment(sketch, "E420", {"start": v(-54.9, -46.12) * mm, "end": v(-54.9, -46.92) * mm});
            skLineSegment(sketch, "E421", {"start": v(-54.9, -46.92) * mm, "end": v(-55.3, -46.92) * mm});
            skLineSegment(sketch, "E422", {"start": v(-60, -34.22) * mm, "end": v(-60, -33.82) * mm});
            skLineSegment(sketch, "E423", {"start": v(-60, -33.82) * mm, "end": v(-59.2, -33.82) * mm});
            skLineSegment(sketch, "E424", {"start": v(-59.2, -33.82) * mm, "end": v(-59.2, -34.22) * mm});
            skLineSegment(sketch, "E425", {"start": v(-59.2, -34.22) * mm, "end": v(-60, -34.22) * mm});
            skLineSegment(sketch, "E426", {"start": v(-55.3, -34.92) * mm, "end": v(-55.3, -34.12) * mm});
            skLineSegment(sketch, "E427", {"start": v(-55.3, -34.12) * mm, "end": v(-54.9, -34.12) * mm});
            skLineSegment(sketch, "E428", {"start": v(-54.9, -34.12) * mm, "end": v(-54.9, -34.92) * mm});
            skLineSegment(sketch, "E429", {"start": v(-54.9, -34.92) * mm, "end": v(-55.3, -34.92) * mm});
            skLineSegment(sketch, "E430", {"start": v(-59.4, -38.62) * mm, "end": v(-59.4, -37.82) * mm});
            skLineSegment(sketch, "E431", {"start": v(-59.4, -37.82) * mm, "end": v(-59, -37.82) * mm});
            skLineSegment(sketch, "E432", {"start": v(-59, -37.82) * mm, "end": v(-59, -38.62) * mm});
            skLineSegment(sketch, "E433", {"start": v(-59, -38.62) * mm, "end": v(-59.4, -38.62) * mm});
            skLineSegment(sketch, "E434", {"start": v(-55.3, -39.92) * mm, "end": v(-55.3, -39.12) * mm});
            skLineSegment(sketch, "E435", {"start": v(-55.3, -39.12) * mm, "end": v(-54.9, -39.12) * mm});
            skLineSegment(sketch, "E436", {"start": v(-54.9, -39.12) * mm, "end": v(-54.9, -39.92) * mm});
            skLineSegment(sketch, "E437", {"start": v(-54.9, -39.92) * mm, "end": v(-55.3, -39.92) * mm});
            skLineSegment(sketch, "E438", {"start": v(-49, -46.92) * mm, "end": v(-49, -46.12) * mm});
            skLineSegment(sketch, "E439", {"start": v(-49, -46.12) * mm, "end": v(-48.6, -46.12) * mm});
            skLineSegment(sketch, "E440", {"start": v(-48.6, -46.12) * mm, "end": v(-48.6, -46.92) * mm});
            skLineSegment(sketch, "E441", {"start": v(-48.6, -46.92) * mm, "end": v(-49, -46.92) * mm});
            skLineSegment(sketch, "E442", {"start": v(-49, -39.92) * mm, "end": v(-49, -39.12) * mm});
            skLineSegment(sketch, "E443", {"start": v(-49, -39.12) * mm, "end": v(-48.6, -39.12) * mm});
            skLineSegment(sketch, "E444", {"start": v(-48.6, -39.12) * mm, "end": v(-48.6, -39.92) * mm});
            skLineSegment(sketch, "E445", {"start": v(-48.6, -39.92) * mm, "end": v(-49, -39.92) * mm});
            skLineSegment(sketch, "E446", {"start": v(-49, -34.92) * mm, "end": v(-49, -34.12) * mm});
            skLineSegment(sketch, "E447", {"start": v(-49, -34.12) * mm, "end": v(-48.6, -34.12) * mm});
            skLineSegment(sketch, "E448", {"start": v(-48.6, -34.12) * mm, "end": v(-48.6, -34.92) * mm});
            skLineSegment(sketch, "E449", {"start": v(-48.6, -34.92) * mm, "end": v(-49, -34.92) * mm});
            skLineSegment(sketch, "E450", {"start": v(-49.3, -29.02) * mm, "end": v(-49.3, -29.42) * mm});
            skLineSegment(sketch, "E451", {"start": v(-49.3, -29.42) * mm, "end": v(-48.5, -29.42) * mm});
            skLineSegment(sketch, "E452", {"start": v(-48.5, -29.42) * mm, "end": v(-48.5, -29.02) * mm});
            skLineSegment(sketch, "E453", {"start": v(-48.5, -29.02) * mm, "end": v(-49.3, -29.02) * mm});
            skLineSegment(sketch, "E454", {"start": v(-40.61, -39.02) * mm, "end": v(-40.61, -39.92) * mm});
            skLineSegment(sketch, "E455", {"start": v(-40.61, -39.92) * mm, "end": v(-40.11, -39.92) * mm});
            skLineSegment(sketch, "E456", {"start": v(-40.11, -39.92) * mm, "end": v(-40.11, -39.02) * mm});
            skLineSegment(sketch, "E457", {"start": v(-40.11, -39.02) * mm, "end": v(-40.61, -39.02) * mm});
            skLineSegment(sketch, "E458", {"start": v(-42.48, -47.7) * mm, "end": v(-42.48, -46.8) * mm});
            skLineSegment(sketch, "E459", {"start": v(-42.48, -46.8) * mm, "end": v(-41.98, -46.8) * mm});
            skLineSegment(sketch, "E460", {"start": v(-41.98, -46.8) * mm, "end": v(-41.98, -47.7) * mm});
            skLineSegment(sketch, "E461", {"start": v(-41.98, -47.7) * mm, "end": v(-42.48, -47.7) * mm});
            skLineSegment(sketch, "E462", {"start": v(-40.46, -35.44) * mm, "end": v(-40.21, -35.44) * mm});
            skLineSegment(sketch, "E463", {"start": v(-40.21, -35.44) * mm, "end": v(-40.2, -24.53) * mm});
            skLineSegment(sketch, "E464", {"start": v(-40.2, -24.53) * mm, "end": v(-39.94, -24.24) * mm});
            skArc(sketch, "E465", {"start": v(-48.24, -15.25) * mm, "mid": v(-44.31, -19.95) * mm, "end": v(-39.94, -24.24) * mm});
            skLineSegment(sketch, "E466", {"start": v(-48.24, -15.25) * mm, "end": v(-43.04, -11.19) * mm});
            skLineSegment(sketch, "E467", {"start": v(-43.04, -11.19) * mm, "end": v(-41.87, -12.7) * mm});
            skArc(sketch, "E468", {"start": v(-41.87, -12.7) * mm, "mid": v(-41.9, -13.24) * mm, "end": v(-41.36, -13.3) * mm});
            skArc(sketch, "E469", {"start": v(-41.36, -13.3) * mm, "mid": v(-37.95, -17.06) * mm, "end": v(-34.2, -20.47) * mm});
            skArc(sketch, "E470", {"start": v(-34.2, -20.47) * mm, "mid": v(-34.13, -21.02) * mm, "end": v(-33.58, -20.98) * mm});
            skLineSegment(sketch, "E471", {"start": v(-33.58, -20.98) * mm, "end": v(-33.5, -21.04) * mm});
            skLineSegment(sketch, "E472", {"start": v(-33.5, -21.04) * mm, "end": v(-33.5, -35.44) * mm});
            skLineSegment(sketch, "E473", {"start": v(-33.5, -35.44) * mm, "end": v(-33.26, -35.44) * mm});
            skLineSegment(sketch, "E474", {"start": v(-33.26, -35.44) * mm, "end": v(-33.26, -30.6) * mm});
            skArc(sketch, "E475", {"start": v(-33.26, -30.6) * mm, "mid": v(-29.4, -32.94) * mm, "end": v(-25.37, -35) * mm});
            skLineSegment(sketch, "E476", {"start": v(-25.37, -35) * mm, "end": v(-25.24, -34.73) * mm});
            skArc(sketch, "E477", {"start": v(-27.96, -33.38) * mm, "mid": v(-26.6, -34.07) * mm, "end": v(-25.24, -34.73) * mm});
            skLineSegment(sketch, "E478", {"start": v(-27.96, -33.38) * mm, "end": v(-27.63, -32.76) * mm});
            skLineSegment(sketch, "E479", {"start": v(-27.63, -32.76) * mm, "end": v(-28.07, -32.53) * mm});
            skLineSegment(sketch, "E480", {"start": v(-28.07, -32.53) * mm, "end": v(-28.4, -33.15) * mm});
            skArc(sketch, "E481", {"start": v(-32.92, -30.47) * mm, "mid": v(-30.69, -31.85) * mm, "end": v(-28.4, -33.15) * mm});
            skLineSegment(sketch, "E482", {"start": v(-32.92, -30.47) * mm, "end": v(-32.54, -29.88) * mm});
            skLineSegment(sketch, "E483", {"start": v(-32.54, -29.88) * mm, "end": v(-33.26, -29.41) * mm});
            skLineSegment(sketch, "E484", {"start": v(-33.26, -29.41) * mm, "end": v(-33.26, -20.92) * mm});
            skLineSegment(sketch, "E485", {"start": v(-33.26, -20.92) * mm, "end": v(-33.48, -20.74) * mm});
            skArc(sketch, "E486", {"start": v(-33.48, -20.74) * mm, "mid": v(-33.62, -20.4) * mm, "end": v(-33.99, -20.32) * mm});
            skArc(sketch, "E487", {"start": v(-37.56, -17.09) * mm, "mid": v(-35.8, -18.75) * mm, "end": v(-33.99, -20.32) * mm});
            skLineSegment(sketch, "E488", {"start": v(-37.56, -17.09) * mm, "end": v(-37.31, -16.85) * mm});
            skLineSegment(sketch, "E489", {"start": v(-37.31, -16.85) * mm, "end": v(-37.74, -16.42) * mm});
            skLineSegment(sketch, "E490", {"start": v(-37.74, -16.42) * mm, "end": v(-37.98, -16.67) * mm});
            skArc(sketch, "E491", {"start": v(-41.22, -13.1) * mm, "mid": v(-39.64, -14.92) * mm, "end": v(-37.98, -16.67) * mm});
            skArc(sketch, "E492", {"start": v(-41.22, -13.1) * mm, "mid": v(-41.29, -12.73) * mm, "end": v(-41.63, -12.59) * mm});
            skArc(sketch, "E493", {"start": v(-43, -10.84) * mm, "mid": v(-42.32, -11.72) * mm, "end": v(-41.63, -12.59) * mm});
            skLineSegment(sketch, "E494", {"start": v(-43, -10.84) * mm, "end": v(-48.6, -15.2) * mm});
            skArc(sketch, "E495", {"start": v(-48.6, -15.2) * mm, "mid": v(-47.19, -17) * mm, "end": v(-45.72, -18.76) * mm});
            skLineSegment(sketch, "E496", {"start": v(-45.72, -18.76) * mm, "end": v(-47.6, -20.4) * mm});
            skLineSegment(sketch, "E497", {"start": v(-47.6, -20.4) * mm, "end": v(-44.7, -23.52) * mm});
            skLineSegment(sketch, "E498", {"start": v(-44.7, -23.52) * mm, "end": v(-46.27, -25.1) * mm});
            skLineSegment(sketch, "E499", {"start": v(-42.41, -28.68) * mm, "end": v(-42.8, -29.52) * mm});
            skLineSegment(sketch, "E500", {"start": v(-42.8, -29.52) * mm, "end": v(-42.35, -29.73) * mm});
            skLineSegment(sketch, "E501", {"start": v(-42.35, -29.73) * mm, "end": v(-42.02, -29.02) * mm});
            skLineSegment(sketch, "E502", {"start": v(-42.02, -29.02) * mm, "end": v(-40.46, -30.3) * mm});
            skLineSegment(sketch, "E503", {"start": v(-40.46, -30.3) * mm, "end": v(-40.46, -34.12) * mm});
            skLineSegment(sketch, "E504", {"start": v(-40.46, -34.12) * mm, "end": v(-40.61, -34.12) * mm});
            skLineSegment(sketch, "E505", {"start": v(-40.61, -34.12) * mm, "end": v(-40.61, -34.92) * mm});
            skLineSegment(sketch, "E506", {"start": v(-40.61, -34.92) * mm, "end": v(-40.46, -34.92) * mm});
            skLineSegment(sketch, "E507", {"start": v(-40.46, -34.92) * mm, "end": v(-40.46, -35.44) * mm});
            skArc(sketch, "E508", {"start": v(-46.27, -25.1) * mm, "mid": v(-44.38, -26.93) * mm, "end": v(-42.41, -28.68) * mm});
            skLineSegment(sketch, "E509", {"start": v(-31.36, -39.02) * mm, "end": v(-31.36, -39.92) * mm});
            skLineSegment(sketch, "E510", {"start": v(-31.36, -39.92) * mm, "end": v(-30.86, -39.92) * mm});
            skLineSegment(sketch, "E511", {"start": v(-30.86, -39.92) * mm, "end": v(-30.86, -39.02) * mm});
            skLineSegment(sketch, "E512", {"start": v(-30.86, -39.02) * mm, "end": v(-31.36, -39.02) * mm});
            skLineSegment(sketch, "E513", {"start": v(-26.26, -39.12) * mm, "end": v(-26.26, -39.92) * mm});
            skLineSegment(sketch, "E514", {"start": v(-26.26, -39.92) * mm, "end": v(-25.86, -39.92) * mm});
            skLineSegment(sketch, "E515", {"start": v(-25.86, -39.92) * mm, "end": v(-25.86, -39.12) * mm});
            skLineSegment(sketch, "E516", {"start": v(-25.86, -39.12) * mm, "end": v(-26.26, -39.12) * mm});
            skLineSegment(sketch, "E517", {"start": v(-21.2, -39.12) * mm, "end": v(-21.2, -39.92) * mm});
            skLineSegment(sketch, "E518", {"start": v(-21.2, -39.92) * mm, "end": v(-20.8, -39.92) * mm});
            skLineSegment(sketch, "E519", {"start": v(-20.8, -39.92) * mm, "end": v(-20.8, -39.12) * mm});
            skLineSegment(sketch, "E520", {"start": v(-20.8, -39.12) * mm, "end": v(-21.2, -39.12) * mm});
            skLineSegment(sketch, "E521", {"start": v(1.07, -47.3) * mm, "end": v(1.07, -48.2) * mm});
            skLineSegment(sketch, "E522", {"start": v(1.07, -48.2) * mm, "end": v(1.57, -48.2) * mm});
            skLineSegment(sketch, "E523", {"start": v(1.57, -48.2) * mm, "end": v(1.57, -47.3) * mm});
            skLineSegment(sketch, "E524", {"start": v(1.57, -47.3) * mm, "end": v(1.07, -47.3) * mm});
            skLineSegment(sketch, "E525", {"start": v(7.96, -47.3) * mm, "end": v(7.96, -48.2) * mm});
            skLineSegment(sketch, "E526", {"start": v(7.96, -48.2) * mm, "end": v(8.46, -48.2) * mm});
            skLineSegment(sketch, "E527", {"start": v(8.46, -48.2) * mm, "end": v(8.46, -47.3) * mm});
            skLineSegment(sketch, "E528", {"start": v(8.46, -47.3) * mm, "end": v(7.96, -47.3) * mm});
            skLineSegment(sketch, "E529", {"start": v(15.42, -39.12) * mm, "end": v(15.42, -40.02) * mm});
            skLineSegment(sketch, "E530", {"start": v(15.42, -40.02) * mm, "end": v(15.92, -40.02) * mm});
            skLineSegment(sketch, "E531", {"start": v(15.92, -40.02) * mm, "end": v(15.92, -39.12) * mm});
            skLineSegment(sketch, "E532", {"start": v(15.92, -39.12) * mm, "end": v(15.42, -39.12) * mm});
            skLineSegment(sketch, "E533", {"start": v(7.96, -38.92) * mm, "end": v(7.96, -40.02) * mm});
            skLineSegment(sketch, "E534", {"start": v(7.96, -40.02) * mm, "end": v(8.46, -40.02) * mm});
            skLineSegment(sketch, "E535", {"start": v(8.46, -40.02) * mm, "end": v(8.46, -38.92) * mm});
            skLineSegment(sketch, "E536", {"start": v(8.46, -38.92) * mm, "end": v(7.96, -38.92) * mm});
            skLineSegment(sketch, "E537", {"start": v(7.97, -33.1) * mm, "end": v(7.97, -34) * mm});
            skLineSegment(sketch, "E538", {"start": v(7.97, -34) * mm, "end": v(8.47, -34) * mm});
            skLineSegment(sketch, "E539", {"start": v(8.47, -34) * mm, "end": v(8.47, -33.1) * mm});
            skLineSegment(sketch, "E540", {"start": v(8.47, -33.1) * mm, "end": v(7.97, -33.1) * mm});
            skLineSegment(sketch, "E541", {"start": v(15.42, -33.1) * mm, "end": v(15.42, -34) * mm});
            skLineSegment(sketch, "E542", {"start": v(15.42, -34) * mm, "end": v(15.92, -34) * mm});
            skLineSegment(sketch, "E543", {"start": v(15.92, -34) * mm, "end": v(15.92, -33.1) * mm});
            skLineSegment(sketch, "E544", {"start": v(15.92, -33.1) * mm, "end": v(15.42, -33.1) * mm});
            skLineSegment(sketch, "E545", {"start": v(7.97, -27.64) * mm, "end": v(7.97, -28.54) * mm});
            skLineSegment(sketch, "E546", {"start": v(7.97, -28.54) * mm, "end": v(8.47, -28.54) * mm});
            skLineSegment(sketch, "E547", {"start": v(8.47, -28.54) * mm, "end": v(8.47, -27.64) * mm});
            skLineSegment(sketch, "E548", {"start": v(8.47, -27.64) * mm, "end": v(7.97, -27.64) * mm});
            skLineSegment(sketch, "E549", {"start": v(15.42, -27.64) * mm, "end": v(15.42, -28.54) * mm});
            skLineSegment(sketch, "E550", {"start": v(15.42, -28.54) * mm, "end": v(15.92, -28.54) * mm});
            skLineSegment(sketch, "E551", {"start": v(15.92, -28.54) * mm, "end": v(15.92, -27.64) * mm});
            skLineSegment(sketch, "E552", {"start": v(15.92, -27.64) * mm, "end": v(15.42, -27.64) * mm});
            skLineSegment(sketch, "E553", {"start": v(1.07, -39.02) * mm, "end": v(1.07, -40.02) * mm});
            skLineSegment(sketch, "E554", {"start": v(1.07, -40.02) * mm, "end": v(1.57, -40.02) * mm});
            skLineSegment(sketch, "E555", {"start": v(1.57, -40.02) * mm, "end": v(1.57, -39.02) * mm});
            skLineSegment(sketch, "E556", {"start": v(1.57, -39.02) * mm, "end": v(1.07, -39.02) * mm});
            skLineSegment(sketch, "E557", {"start": v(1.07, -33.1) * mm, "end": v(1.07, -34) * mm});
            skLineSegment(sketch, "E558", {"start": v(1.07, -34) * mm, "end": v(1.57, -34) * mm});
            skLineSegment(sketch, "E559", {"start": v(1.57, -34) * mm, "end": v(1.57, -33.1) * mm});
            skLineSegment(sketch, "E560", {"start": v(1.57, -33.1) * mm, "end": v(1.07, -33.1) * mm});
            skLineSegment(sketch, "E561", {"start": v(0.97, -27.64) * mm, "end": v(0.97, -28.54) * mm});
            skLineSegment(sketch, "E562", {"start": v(0.97, -28.54) * mm, "end": v(1.47, -28.54) * mm});
            skLineSegment(sketch, "E563", {"start": v(1.47, -28.54) * mm, "end": v(1.47, -27.64) * mm});
            skLineSegment(sketch, "E564", {"start": v(1.47, -27.64) * mm, "end": v(0.97, -27.64) * mm});
            skLineSegment(sketch, "E565", {"start": v(7.97, -20.34) * mm, "end": v(7.97, -21.44) * mm});
            skLineSegment(sketch, "E566", {"start": v(7.97, -21.44) * mm, "end": v(8.47, -21.44) * mm});
            skLineSegment(sketch, "E567", {"start": v(8.47, -21.44) * mm, "end": v(8.47, -20.34) * mm});
            skLineSegment(sketch, "E568", {"start": v(8.47, -20.34) * mm, "end": v(7.97, -20.34) * mm});
            skLineSegment(sketch, "E569", {"start": v(15.42, -20.54) * mm, "end": v(15.42, -21.44) * mm});
            skLineSegment(sketch, "E570", {"start": v(15.42, -21.44) * mm, "end": v(15.92, -21.44) * mm});
            skLineSegment(sketch, "E571", {"start": v(15.92, -21.44) * mm, "end": v(15.92, -20.54) * mm});
            skLineSegment(sketch, "E572", {"start": v(15.92, -20.54) * mm, "end": v(15.42, -20.54) * mm});
            skLineSegment(sketch, "E573", {"start": v(21.84, -20.54) * mm, "end": v(21.84, -21.44) * mm});
            skLineSegment(sketch, "E574", {"start": v(21.84, -21.44) * mm, "end": v(22.34, -21.44) * mm});
            skLineSegment(sketch, "E575", {"start": v(22.34, -21.44) * mm, "end": v(22.34, -20.54) * mm});
            skLineSegment(sketch, "E576", {"start": v(22.34, -20.54) * mm, "end": v(21.84, -20.54) * mm});
            skLineSegment(sketch, "E577", {"start": v(27.77, -20.54) * mm, "end": v(27.77, -21.44) * mm});
            skLineSegment(sketch, "E578", {"start": v(27.77, -21.44) * mm, "end": v(28.27, -21.44) * mm});
            skLineSegment(sketch, "E579", {"start": v(28.27, -21.44) * mm, "end": v(28.27, -20.54) * mm});
            skLineSegment(sketch, "E580", {"start": v(28.27, -20.54) * mm, "end": v(27.77, -20.54) * mm});
            skLineSegment(sketch, "E581", {"start": v(33.84, -20.44) * mm, "end": v(33.84, -21.44) * mm});
            skLineSegment(sketch, "E582", {"start": v(33.84, -21.44) * mm, "end": v(34.34, -21.44) * mm});
            skLineSegment(sketch, "E583", {"start": v(34.34, -21.44) * mm, "end": v(34.34, -20.44) * mm});
            skLineSegment(sketch, "E584", {"start": v(34.34, -20.44) * mm, "end": v(33.84, -20.44) * mm});
            skLineSegment(sketch, "E585", {"start": v(41.84, -20.44) * mm, "end": v(41.84, -21.44) * mm});
            skLineSegment(sketch, "E586", {"start": v(41.84, -21.44) * mm, "end": v(42.64, -21.44) * mm});
            skLineSegment(sketch, "E587", {"start": v(42.64, -21.44) * mm, "end": v(42.64, -20.44) * mm});
            skLineSegment(sketch, "E588", {"start": v(42.64, -20.44) * mm, "end": v(41.84, -20.44) * mm});
            skLineSegment(sketch, "E589", {"start": v(49.9, -20.64) * mm, "end": v(49.9, -21.44) * mm});
            skLineSegment(sketch, "E590", {"start": v(49.9, -21.44) * mm, "end": v(50.3, -21.44) * mm});
            skLineSegment(sketch, "E591", {"start": v(50.3, -21.44) * mm, "end": v(50.3, -20.64) * mm});
            skLineSegment(sketch, "E592", {"start": v(50.3, -20.64) * mm, "end": v(49.9, -20.64) * mm});
            skLineSegment(sketch, "E593", {"start": v(56.24, -20.34) * mm, "end": v(56.24, -21.44) * mm});
            skLineSegment(sketch, "E594", {"start": v(56.24, -21.44) * mm, "end": v(56.84, -21.44) * mm});
            skLineSegment(sketch, "E595", {"start": v(56.84, -21.44) * mm, "end": v(56.84, -20.34) * mm});
            skLineSegment(sketch, "E596", {"start": v(56.84, -20.34) * mm, "end": v(56.24, -20.34) * mm});
            skLineSegment(sketch, "E597", {"start": v(59.52, -20.03) * mm, "end": v(59.52, -20.83) * mm});
            skLineSegment(sketch, "E598", {"start": v(59.52, -20.83) * mm, "end": v(59.92, -20.83) * mm});
            skLineSegment(sketch, "E599", {"start": v(59.92, -20.83) * mm, "end": v(59.92, -20.03) * mm});
            skLineSegment(sketch, "E600", {"start": v(59.92, -20.03) * mm, "end": v(59.52, -20.03) * mm});
            skLineSegment(sketch, "E601", {"start": v(63.5, -20.44) * mm, "end": v(63.5, -21.04) * mm});
            skLineSegment(sketch, "E602", {"start": v(63.5, -21.04) * mm, "end": v(64.6, -21.04) * mm});
            skLineSegment(sketch, "E603", {"start": v(64.6, -21.04) * mm, "end": v(64.6, -20.44) * mm});
            skLineSegment(sketch, "E604", {"start": v(64.6, -20.44) * mm, "end": v(63.5, -20.44) * mm});
            skLineSegment(sketch, "E605", {"start": v(63.92, -12.84) * mm, "end": v(63.92, -13.64) * mm});
            skLineSegment(sketch, "E606", {"start": v(63.92, -13.64) * mm, "end": v(64.52, -13.64) * mm});
            skLineSegment(sketch, "E607", {"start": v(64.52, -13.64) * mm, "end": v(64.52, -12.84) * mm});
            skLineSegment(sketch, "E608", {"start": v(64.52, -12.84) * mm, "end": v(63.92, -12.84) * mm});
            skLineSegment(sketch, "E609", {"start": v(63.5, -28.14) * mm, "end": v(63.5, -28.74) * mm});
            skLineSegment(sketch, "E610", {"start": v(63.5, -28.74) * mm, "end": v(64.6, -28.74) * mm});
            skLineSegment(sketch, "E611", {"start": v(64.6, -28.74) * mm, "end": v(64.6, -28.14) * mm});
            skLineSegment(sketch, "E612", {"start": v(64.6, -28.14) * mm, "end": v(63.5, -28.14) * mm});
            skLineSegment(sketch, "E613", {"start": v(71.17, -28.24) * mm, "end": v(71.17, -28.74) * mm});
            skLineSegment(sketch, "E614", {"start": v(71.17, -28.74) * mm, "end": v(72.07, -28.74) * mm});
            skLineSegment(sketch, "E615", {"start": v(72.07, -28.74) * mm, "end": v(72.07, -28.24) * mm});
            skLineSegment(sketch, "E616", {"start": v(72.07, -28.24) * mm, "end": v(71.17, -28.24) * mm});
            skLineSegment(sketch, "E617", {"start": v(71.17, -36.44) * mm, "end": v(71.17, -36.94) * mm});
            skLineSegment(sketch, "E618", {"start": v(71.17, -36.94) * mm, "end": v(72.07, -36.94) * mm});
            skLineSegment(sketch, "E619", {"start": v(72.07, -36.94) * mm, "end": v(72.07, -36.44) * mm});
            skLineSegment(sketch, "E620", {"start": v(72.07, -36.44) * mm, "end": v(71.17, -36.44) * mm});
            skLineSegment(sketch, "E621", {"start": v(63.7, -36.44) * mm, "end": v(63.7, -36.94) * mm});
            skLineSegment(sketch, "E622", {"start": v(63.7, -36.94) * mm, "end": v(64.6, -36.94) * mm});
            skLineSegment(sketch, "E623", {"start": v(64.6, -36.94) * mm, "end": v(64.6, -36.44) * mm});
            skLineSegment(sketch, "E624", {"start": v(64.6, -36.44) * mm, "end": v(63.7, -36.44) * mm});
            skLineSegment(sketch, "E625", {"start": v(63.7, -39.6) * mm, "end": v(63.7, -40.1) * mm});
            skLineSegment(sketch, "E626", {"start": v(63.7, -40.1) * mm, "end": v(64.6, -40.1) * mm});
            skLineSegment(sketch, "E627", {"start": v(64.6, -40.1) * mm, "end": v(64.6, -39.6) * mm});
            skLineSegment(sketch, "E628", {"start": v(64.6, -39.6) * mm, "end": v(63.7, -39.6) * mm});
            skLineSegment(sketch, "E629", {"start": v(71.17, -42.44) * mm, "end": v(71.17, -41.94) * mm});
            skLineSegment(sketch, "E630", {"start": v(71.17, -41.94) * mm, "end": v(72.07, -41.94) * mm});
            skLineSegment(sketch, "E631", {"start": v(72.07, -41.94) * mm, "end": v(72.07, -42.44) * mm});
            skLineSegment(sketch, "E632", {"start": v(72.07, -42.44) * mm, "end": v(71.17, -42.44) * mm});
            skLineSegment(sketch, "E633", {"start": v(41.84, -40.12) * mm, "end": v(41.84, -39.12) * mm});
            skLineSegment(sketch, "E634", {"start": v(41.84, -39.12) * mm, "end": v(42.64, -39.12) * mm});
            skLineSegment(sketch, "E635", {"start": v(42.64, -39.12) * mm, "end": v(42.64, -40.12) * mm});
            skLineSegment(sketch, "E636", {"start": v(42.64, -40.12) * mm, "end": v(41.84, -40.12) * mm});
            skLineSegment(sketch, "E637", {"start": v(49.9, -39.32) * mm, "end": v(49.9, -40.12) * mm});
            skLineSegment(sketch, "E638", {"start": v(49.9, -40.12) * mm, "end": v(50.3, -40.12) * mm});
            skLineSegment(sketch, "E639", {"start": v(50.3, -40.12) * mm, "end": v(50.3, -39.32) * mm});
            skLineSegment(sketch, "E640", {"start": v(50.3, -39.32) * mm, "end": v(49.9, -39.32) * mm});
            skLineSegment(sketch, "E641", {"start": v(56.24, -39.02) * mm, "end": v(56.24, -40.12) * mm});
            skLineSegment(sketch, "E642", {"start": v(56.24, -40.12) * mm, "end": v(56.84, -40.12) * mm});
            skLineSegment(sketch, "E643", {"start": v(56.84, -40.12) * mm, "end": v(56.84, -39.02) * mm});
            skLineSegment(sketch, "E644", {"start": v(56.84, -39.02) * mm, "end": v(56.24, -39.02) * mm});
            skLineSegment(sketch, "E645", {"start": v(49.8, -33.1) * mm, "end": v(49.8, -33.9) * mm});
            skLineSegment(sketch, "E646", {"start": v(49.8, -33.9) * mm, "end": v(50.6, -33.9) * mm});
            skLineSegment(sketch, "E647", {"start": v(50.6, -33.9) * mm, "end": v(50.6, -33.1) * mm});
            skLineSegment(sketch, "E648", {"start": v(50.6, -33.1) * mm, "end": v(49.8, -33.1) * mm});
            skLineSegment(sketch, "E649", {"start": v(41.84, -34.1) * mm, "end": v(41.84, -33.1) * mm});
            skLineSegment(sketch, "E650", {"start": v(41.84, -33.1) * mm, "end": v(42.34, -33.1) * mm});
            skLineSegment(sketch, "E651", {"start": v(42.34, -33.1) * mm, "end": v(42.34, -34.1) * mm});
            skLineSegment(sketch, "E652", {"start": v(42.34, -34.1) * mm, "end": v(41.84, -34.1) * mm});
            skLineSegment(sketch, "E653", {"start": v(41.84, -28.44) * mm, "end": v(41.84, -27.44) * mm});
            skLineSegment(sketch, "E654", {"start": v(41.84, -27.44) * mm, "end": v(42.34, -27.44) * mm});
            skLineSegment(sketch, "E655", {"start": v(42.34, -27.44) * mm, "end": v(42.34, -28.44) * mm});
            skLineSegment(sketch, "E656", {"start": v(42.34, -28.44) * mm, "end": v(41.84, -28.44) * mm});
            skLineSegment(sketch, "E657", {"start": v(49.8, -27.54) * mm, "end": v(49.8, -28.34) * mm});
            skLineSegment(sketch, "E658", {"start": v(49.8, -28.34) * mm, "end": v(50.6, -28.34) * mm});
            skLineSegment(sketch, "E659", {"start": v(50.6, -28.34) * mm, "end": v(50.6, -27.54) * mm});
            skLineSegment(sketch, "E660", {"start": v(50.6, -27.54) * mm, "end": v(49.8, -27.54) * mm});
            skLineSegment(sketch, "E661", {"start": v(49.84, -48.2) * mm, "end": v(49.84, -47.4) * mm});
            skLineSegment(sketch, "E662", {"start": v(49.84, -47.4) * mm, "end": v(50.64, -47.4) * mm});
            skLineSegment(sketch, "E663", {"start": v(50.64, -47.4) * mm, "end": v(50.64, -48.2) * mm});
            skLineSegment(sketch, "E664", {"start": v(50.64, -48.2) * mm, "end": v(49.84, -48.2) * mm});
            skLineSegment(sketch, "E665", {"start": v(56.34, -48.2) * mm, "end": v(56.34, -47.1) * mm});
            skLineSegment(sketch, "E666", {"start": v(56.34, -47.1) * mm, "end": v(56.84, -47.1) * mm});
            skLineSegment(sketch, "E667", {"start": v(56.84, -47.1) * mm, "end": v(56.84, -48.2) * mm});
            skLineSegment(sketch, "E668", {"start": v(56.84, -48.2) * mm, "end": v(56.34, -48.2) * mm});
            skLineSegment(sketch, "E669", {"start": v(34.84, -40.12) * mm, "end": v(34.84, -39.02) * mm});
            skLineSegment(sketch, "E670", {"start": v(34.84, -39.02) * mm, "end": v(35.34, -39.02) * mm});
            skLineSegment(sketch, "E671", {"start": v(35.34, -39.02) * mm, "end": v(35.34, -40.12) * mm});
            skLineSegment(sketch, "E672", {"start": v(35.34, -40.12) * mm, "end": v(34.84, -40.12) * mm});
            skLineSegment(sketch, "E673", {"start": v(34.84, -34) * mm, "end": v(34.84, -33.1) * mm});
            skLineSegment(sketch, "E674", {"start": v(34.84, -33.1) * mm, "end": v(35.34, -33.1) * mm});
            skLineSegment(sketch, "E675", {"start": v(35.34, -33.1) * mm, "end": v(35.34, -34) * mm});
            skLineSegment(sketch, "E676", {"start": v(35.34, -34) * mm, "end": v(34.84, -34) * mm});
            skLineSegment(sketch, "E677", {"start": v(34.84, -28.34) * mm, "end": v(34.84, -27.44) * mm});
            skLineSegment(sketch, "E678", {"start": v(34.84, -27.44) * mm, "end": v(35.34, -27.44) * mm});
            skLineSegment(sketch, "E679", {"start": v(35.34, -27.44) * mm, "end": v(35.34, -28.34) * mm});
            skLineSegment(sketch, "E680", {"start": v(35.34, -28.34) * mm, "end": v(34.84, -28.34) * mm});
            skLineSegment(sketch, "E681", {"start": v(25.72, -34) * mm, "end": v(25.72, -33.4) * mm});
            skLineSegment(sketch, "E682", {"start": v(25.72, -33.4) * mm, "end": v(26.32, -33.4) * mm});
            skLineSegment(sketch, "E683", {"start": v(26.32, -33.4) * mm, "end": v(26.32, -34) * mm});
            skLineSegment(sketch, "E684", {"start": v(26.32, -34) * mm, "end": v(25.72, -34) * mm});
            skLineSegment(sketch, "E685", {"start": v(25.72, -28.2) * mm, "end": v(25.72, -27.6) * mm});
            skLineSegment(sketch, "E686", {"start": v(25.72, -27.6) * mm, "end": v(26.32, -27.6) * mm});
            skLineSegment(sketch, "E687", {"start": v(26.32, -27.6) * mm, "end": v(26.32, -28.2) * mm});
            skLineSegment(sketch, "E688", {"start": v(26.32, -28.2) * mm, "end": v(25.72, -28.2) * mm});
            skCircle(sketch, "E689", {"center": v(21.46, -33.7) * mm, "radius": 0.35 * mm});
            skCircle(sketch, "E690", {"center": v(30.57, -33.7) * mm, "radius": 0.35 * mm});
            skCircle(sketch, "E691", {"center": v(21.46, -27.9) * mm, "radius": 0.35 * mm});
            skCircle(sketch, "E692", {"center": v(30.57, -27.9) * mm, "radius": 0.35 * mm});
            skLineSegment(sketch, "E693", {"start": v(71.17, 11.1) * mm, "end": v(71.17, 11.6) * mm});
            skLineSegment(sketch, "E694", {"start": v(71.17, 11.6) * mm, "end": v(72.07, 11.6) * mm});
            skLineSegment(sketch, "E695", {"start": v(72.07, 11.6) * mm, "end": v(72.07, 11.1) * mm});
            skLineSegment(sketch, "E696", {"start": v(72.07, 11.1) * mm, "end": v(71.17, 11.1) * mm});
            skLineSegment(sketch, "E697", {"start": v(63.62, 12.4) * mm, "end": v(63.62, 13) * mm});
            skLineSegment(sketch, "E698", {"start": v(63.62, 13) * mm, "end": v(64.62, 13) * mm});
            skLineSegment(sketch, "E699", {"start": v(64.62, 13) * mm, "end": v(64.62, 12.4) * mm});
            skLineSegment(sketch, "E700", {"start": v(64.62, 12.4) * mm, "end": v(63.62, 12.4) * mm});
            skLineSegment(sketch, "E701", {"start": v(64.42, 36.26) * mm, "end": v(64.42, 35.46) * mm});
            skLineSegment(sketch, "E702", {"start": v(64.42, 35.46) * mm, "end": v(65.22, 35.46) * mm});
            skLineSegment(sketch, "E703", {"start": v(65.22, 35.46) * mm, "end": v(65.22, 36.26) * mm});
            skLineSegment(sketch, "E704", {"start": v(65.22, 36.26) * mm, "end": v(64.42, 36.26) * mm});
            skLineSegment(sketch, "E705", {"start": v(64.42, 31.68) * mm, "end": v(64.42, 30.88) * mm});
            skLineSegment(sketch, "E706", {"start": v(64.42, 30.88) * mm, "end": v(65.22, 30.88) * mm});
            skLineSegment(sketch, "E707", {"start": v(65.22, 30.88) * mm, "end": v(65.22, 31.68) * mm});
            skLineSegment(sketch, "E708", {"start": v(65.22, 31.68) * mm, "end": v(64.42, 31.68) * mm});
            skLineSegment(sketch, "E709", {"start": v(59.6, 35.36) * mm, "end": v(59.6, 36.16) * mm});
            skLineSegment(sketch, "E710", {"start": v(59.6, 36.16) * mm, "end": v(60.4, 36.16) * mm});
            skLineSegment(sketch, "E711", {"start": v(60.4, 36.16) * mm, "end": v(60.4, 35.36) * mm});
            skLineSegment(sketch, "E712", {"start": v(60.4, 35.36) * mm, "end": v(59.6, 35.36) * mm});
            skLineSegment(sketch, "E713", {"start": v(38.54, 36.36) * mm, "end": v(38.54, 35.56) * mm});
            skLineSegment(sketch, "E714", {"start": v(38.54, 35.56) * mm, "end": v(37.74, 35.56) * mm});
            skLineSegment(sketch, "E715", {"start": v(37.74, 35.56) * mm, "end": v(37.74, 36.36) * mm});
            skLineSegment(sketch, "E716", {"start": v(37.74, 36.36) * mm, "end": v(38.54, 36.36) * mm});
            skLineSegment(sketch, "E717", {"start": v(37.7, 29.7) * mm, "end": v(37.7, 28.9) * mm});
            skLineSegment(sketch, "E718", {"start": v(37.7, 28.9) * mm, "end": v(38.5, 28.9) * mm});
            skLineSegment(sketch, "E719", {"start": v(38.5, 28.9) * mm, "end": v(38.5, 29.7) * mm});
            skLineSegment(sketch, "E720", {"start": v(38.5, 29.7) * mm, "end": v(37.7, 29.7) * mm});
            skLineSegment(sketch, "E721", {"start": v(37.7, 25.33) * mm, "end": v(37.7, 24.53) * mm});
            skLineSegment(sketch, "E722", {"start": v(37.7, 24.53) * mm, "end": v(38.5, 24.53) * mm});
            skLineSegment(sketch, "E723", {"start": v(38.5, 24.53) * mm, "end": v(38.5, 25.33) * mm});
            skLineSegment(sketch, "E724", {"start": v(38.5, 25.33) * mm, "end": v(37.7, 25.33) * mm});
            skLineSegment(sketch, "E725", {"start": v(37.7, 20.2) * mm, "end": v(37.7, 19.4) * mm});
            skLineSegment(sketch, "E726", {"start": v(37.7, 19.4) * mm, "end": v(38.5, 19.4) * mm});
            skLineSegment(sketch, "E727", {"start": v(38.5, 19.4) * mm, "end": v(38.5, 20.2) * mm});
            skLineSegment(sketch, "E728", {"start": v(38.5, 20.2) * mm, "end": v(37.7, 20.2) * mm});
            skLineSegment(sketch, "E729", {"start": v(45.7, 19.4) * mm, "end": v(45.7, 20.2) * mm});
            skLineSegment(sketch, "E730", {"start": v(45.7, 20.2) * mm, "end": v(46.5, 20.2) * mm});
            skLineSegment(sketch, "E731", {"start": v(46.5, 20.2) * mm, "end": v(46.5, 19.4) * mm});
            skLineSegment(sketch, "E732", {"start": v(46.5, 19.4) * mm, "end": v(45.7, 19.4) * mm});
            skLineSegment(sketch, "E733", {"start": v(53.7, 25.33) * mm, "end": v(53.7, 24.53) * mm});
            skLineSegment(sketch, "E734", {"start": v(53.7, 24.53) * mm, "end": v(54.5, 24.53) * mm});
            skLineSegment(sketch, "E735", {"start": v(54.5, 24.53) * mm, "end": v(54.5, 25.33) * mm});
            skLineSegment(sketch, "E736", {"start": v(54.5, 25.33) * mm, "end": v(53.7, 25.33) * mm});
            skLineSegment(sketch, "E737", {"start": v(53.7, 20.2) * mm, "end": v(53.7, 19.4) * mm});
            skLineSegment(sketch, "E738", {"start": v(53.7, 19.4) * mm, "end": v(54.5, 19.4) * mm});
            skLineSegment(sketch, "E739", {"start": v(54.5, 19.4) * mm, "end": v(54.5, 20.2) * mm});
            skLineSegment(sketch, "E740", {"start": v(54.5, 20.2) * mm, "end": v(53.7, 20.2) * mm});
            skLineSegment(sketch, "E741", {"start": v(30.14, 21.98) * mm, "end": v(30.14, 22.78) * mm});
            skLineSegment(sketch, "E742", {"start": v(30.14, 22.78) * mm, "end": v(30.94, 22.78) * mm});
            skLineSegment(sketch, "E743", {"start": v(30.94, 22.78) * mm, "end": v(30.94, 21.98) * mm});
            skLineSegment(sketch, "E744", {"start": v(30.94, 21.98) * mm, "end": v(30.14, 21.98) * mm});
            skLineSegment(sketch, "E745", {"start": v(30.14, 25.33) * mm, "end": v(30.14, 24.53) * mm});
            skLineSegment(sketch, "E746", {"start": v(30.14, 24.53) * mm, "end": v(30.94, 24.53) * mm});
            skLineSegment(sketch, "E747", {"start": v(30.94, 24.53) * mm, "end": v(30.94, 25.33) * mm});
            skLineSegment(sketch, "E748", {"start": v(30.94, 25.33) * mm, "end": v(30.14, 25.33) * mm});
            skLineSegment(sketch, "E749", {"start": v(30.14, 31.68) * mm, "end": v(30.14, 30.88) * mm});
            skLineSegment(sketch, "E750", {"start": v(30.14, 30.88) * mm, "end": v(30.94, 30.88) * mm});
            skLineSegment(sketch, "E751", {"start": v(30.94, 30.88) * mm, "end": v(30.94, 31.68) * mm});
            skLineSegment(sketch, "E752", {"start": v(30.94, 31.68) * mm, "end": v(30.14, 31.68) * mm});
            skLineSegment(sketch, "E753", {"start": v(30.14, 36.26) * mm, "end": v(30.14, 35.46) * mm});
            skLineSegment(sketch, "E754", {"start": v(30.14, 35.46) * mm, "end": v(30.94, 35.46) * mm});
            skLineSegment(sketch, "E755", {"start": v(30.94, 35.46) * mm, "end": v(30.94, 36.26) * mm});
            skLineSegment(sketch, "E756", {"start": v(30.94, 36.26) * mm, "end": v(30.14, 36.26) * mm});
            skLineSegment(sketch, "E757", {"start": v(30.94, 42.16) * mm, "end": v(30.94, 42.96) * mm});
            skLineSegment(sketch, "E758", {"start": v(30.94, 42.96) * mm, "end": v(30.14, 42.96) * mm});
            skLineSegment(sketch, "E759", {"start": v(30.14, 42.96) * mm, "end": v(30.14, 42.16) * mm});
            skLineSegment(sketch, "E760", {"start": v(30.14, 42.16) * mm, "end": v(30.94, 42.16) * mm});
            skLineSegment(sketch, "E761", {"start": v(37.7, 42.96) * mm, "end": v(37.7, 42.16) * mm});
            skLineSegment(sketch, "E762", {"start": v(37.7, 42.16) * mm, "end": v(38.5, 42.16) * mm});
            skLineSegment(sketch, "E763", {"start": v(38.5, 42.16) * mm, "end": v(38.5, 42.96) * mm});
            skLineSegment(sketch, "E764", {"start": v(38.5, 42.96) * mm, "end": v(37.7, 42.96) * mm});
            skLineSegment(sketch, "E765", {"start": v(45.7, 42.96) * mm, "end": v(45.7, 42.16) * mm});
            skLineSegment(sketch, "E766", {"start": v(45.7, 42.16) * mm, "end": v(46.5, 42.16) * mm});
            skLineSegment(sketch, "E767", {"start": v(46.5, 42.16) * mm, "end": v(46.5, 42.96) * mm});
            skLineSegment(sketch, "E768", {"start": v(46.5, 42.96) * mm, "end": v(45.7, 42.96) * mm});
            skLineSegment(sketch, "E769", {"start": v(53.7, 42.96) * mm, "end": v(53.7, 42.16) * mm});
            skLineSegment(sketch, "E770", {"start": v(53.7, 42.16) * mm, "end": v(54.5, 42.16) * mm});
            skLineSegment(sketch, "E771", {"start": v(54.5, 42.16) * mm, "end": v(54.5, 42.96) * mm});
            skLineSegment(sketch, "E772", {"start": v(54.5, 42.96) * mm, "end": v(53.7, 42.96) * mm});
            skLineSegment(sketch, "E773", {"start": v(62.1, 42.96) * mm, "end": v(62.1, 42.16) * mm});
            skLineSegment(sketch, "E774", {"start": v(62.1, 42.16) * mm, "end": v(62.9, 42.16) * mm});
            skLineSegment(sketch, "E775", {"start": v(62.9, 42.16) * mm, "end": v(62.9, 42.96) * mm});
            skLineSegment(sketch, "E776", {"start": v(62.9, 42.96) * mm, "end": v(62.1, 42.96) * mm});
            skLineSegment(sketch, "E777", {"start": v(62.1, 43.7) * mm, "end": v(62.1, 43) * mm});
            skLineSegment(sketch, "E778", {"start": v(62.1, 43) * mm, "end": v(62.8, 43) * mm});
            skLineSegment(sketch, "E779", {"start": v(62.8, 43) * mm, "end": v(62.8, 43.7) * mm});
            skLineSegment(sketch, "E780", {"start": v(62.8, 43.7) * mm, "end": v(62.1, 43.7) * mm});
            skLineSegment(sketch, "E781", {"start": v(-14.4, -38.93) * mm, "end": v(-14.16, -37.96) * mm});
            skLineSegment(sketch, "E782", {"start": v(-14.16, -37.96) * mm, "end": v(-13.67, -38.08) * mm});
            skLineSegment(sketch, "E783", {"start": v(-13.67, -38.08) * mm, "end": v(-13.92, -39.05) * mm});
            skLineSegment(sketch, "E784", {"start": v(-13.92, -39.05) * mm, "end": v(-14.4, -38.93) * mm});
            skLineSegment(sketch, "E785", {"start": v(-21.64, -36.6) * mm, "end": v(-21.28, -35.66) * mm});
            skLineSegment(sketch, "E786", {"start": v(-21.28, -35.66) * mm, "end": v(-20.8, -35.84) * mm});
            skLineSegment(sketch, "E787", {"start": v(-20.8, -35.84) * mm, "end": v(-21.17, -36.78) * mm});
            skLineSegment(sketch, "E788", {"start": v(-21.17, -36.78) * mm, "end": v(-21.64, -36.6) * mm});
            skLineSegment(sketch, "E789", {"start": v(-12.72, -32.26) * mm, "end": v(-12.47, -31.3) * mm});
            skLineSegment(sketch, "E790", {"start": v(-12.47, -31.3) * mm, "end": v(-11.99, -31.42) * mm});
            skLineSegment(sketch, "E791", {"start": v(-11.99, -31.42) * mm, "end": v(-12.23, -32.39) * mm});
            skLineSegment(sketch, "E792", {"start": v(-12.23, -32.39) * mm, "end": v(-12.72, -32.26) * mm});
            skLineSegment(sketch, "E793", {"start": v(-7.21, -40.34) * mm, "end": v(-7.08, -39.35) * mm});
            skLineSegment(sketch, "E794", {"start": v(-7.08, -39.35) * mm, "end": v(-6.89, -39.37) * mm});
            skLineSegment(sketch, "E795", {"start": v(-6.89, -39.37) * mm, "end": v(-6.14, -33.55) * mm});
            skLineSegment(sketch, "E796", {"start": v(-6.14, -33.55) * mm, "end": v(-6.34, -33.52) * mm});
            skLineSegment(sketch, "E797", {"start": v(-6.34, -33.52) * mm, "end": v(-6.21, -32.53) * mm});
            skLineSegment(sketch, "E798", {"start": v(-6.21, -32.53) * mm, "end": v(-5.17, -32.66) * mm});
            skLineSegment(sketch, "E799", {"start": v(-5.17, -32.66) * mm, "end": v(-5.3, -33.65) * mm});
            skLineSegment(sketch, "E800", {"start": v(-5.3, -33.65) * mm, "end": v(-5.5, -33.63) * mm});
            skLineSegment(sketch, "E801", {"start": v(-5.5, -33.63) * mm, "end": v(-6.24, -39.46) * mm});
            skLineSegment(sketch, "E802", {"start": v(-6.24, -39.46) * mm, "end": v(-6.04, -39.48) * mm});
            skLineSegment(sketch, "E803", {"start": v(-6.04, -39.48) * mm, "end": v(-6.17, -40.47) * mm});
            skLineSegment(sketch, "E804", {"start": v(-6.17, -40.47) * mm, "end": v(-7.21, -40.34) * mm});
            skLineSegment(sketch, "E805", {"start": v(-5.51, -27.07) * mm, "end": v(-5.02, -27.14) * mm});
            skLineSegment(sketch, "E806", {"start": v(-5.02, -27.14) * mm, "end": v(-5.15, -28.13) * mm});
            skLineSegment(sketch, "E807", {"start": v(-5.15, -28.13) * mm, "end": v(-5.64, -28.07) * mm});
            skLineSegment(sketch, "E808", {"start": v(-5.64, -28.07) * mm, "end": v(-5.51, -27.07) * mm});
            skLineSegment(sketch, "E809", {"start": v(-4.97, -27.14) * mm, "end": v(-4.47, -27.2) * mm});
            skLineSegment(sketch, "E810", {"start": v(-4.47, -27.2) * mm, "end": v(-4.6, -28.2) * mm});
            skLineSegment(sketch, "E811", {"start": v(-4.6, -28.2) * mm, "end": v(-5.1, -28.14) * mm});
            skLineSegment(sketch, "E812", {"start": v(-5.1, -28.14) * mm, "end": v(-4.97, -27.14) * mm});
            skLineSegment(sketch, "E813", {"start": v(-11.12, -25.96) * mm, "end": v(-10.64, -26.09) * mm});
            skLineSegment(sketch, "E814", {"start": v(-10.64, -26.09) * mm, "end": v(-10.88, -27.06) * mm});
            skLineSegment(sketch, "E815", {"start": v(-10.88, -27.06) * mm, "end": v(-11.37, -26.93) * mm});
            skLineSegment(sketch, "E816", {"start": v(-11.37, -26.93) * mm, "end": v(-11.12, -25.96) * mm});
            skLineSegment(sketch, "E817", {"start": v(-16.82, -24.12) * mm, "end": v(-16.36, -24.3) * mm});
            skLineSegment(sketch, "E818", {"start": v(-16.36, -24.3) * mm, "end": v(-16.72, -25.23) * mm});
            skLineSegment(sketch, "E819", {"start": v(-16.72, -25.23) * mm, "end": v(-17.18, -25.05) * mm});
            skLineSegment(sketch, "E820", {"start": v(-17.18, -25.05) * mm, "end": v(-16.82, -24.12) * mm});
            skLineSegment(sketch, "E821", {"start": v(-22.26, -21.6) * mm, "end": v(-21.82, -21.84) * mm});
            skLineSegment(sketch, "E822", {"start": v(-21.82, -21.84) * mm, "end": v(-22.29, -22.72) * mm});
            skLineSegment(sketch, "E823", {"start": v(-22.29, -22.72) * mm, "end": v(-22.73, -22.49) * mm});
            skLineSegment(sketch, "E824", {"start": v(-22.73, -22.49) * mm, "end": v(-22.26, -21.6) * mm});
            skLineSegment(sketch, "E825", {"start": v(-34.62, -13.3) * mm, "end": v(-34.2, -13.71) * mm});
            skLineSegment(sketch, "E826", {"start": v(-34.2, -13.71) * mm, "end": v(-33.77, -13.3) * mm});
            skLineSegment(sketch, "E827", {"start": v(-33.77, -13.3) * mm, "end": v(-34.2, -12.87) * mm});
            skLineSegment(sketch, "E828", {"start": v(-34.2, -12.87) * mm, "end": v(-34.62, -13.3) * mm});
            skCircle(sketch, "E829", {"center": v(-30.52, -17) * mm, "radius": 0.4 * mm});
            skCircle(sketch, "E830", {"center": v(-37.89, -9.63) * mm, "radius": 0.4 * mm});
            skArc(sketch, "E831", {"start": v(-27.6, -31.93) * mm, "mid": v(-24.18, -33.61) * mm, "end": v(-20.67, -35.1) * mm});
            skArc(sketch, "E832", {"start": v(-24.46, -26.8) * mm, "mid": v(-21.69, -28.16) * mm, "end": v(-18.85, -29.37) * mm});
            skLineSegment(sketch, "E833", {"start": v(-24.46, -26.8) * mm, "end": v(-24.4, -26.7) * mm});
            skLineSegment(sketch, "E834", {"start": v(-24.4, -26.7) * mm, "end": v(-24.84, -26.46) * mm});
            skLineSegment(sketch, "E835", {"start": v(-24.84, -26.46) * mm, "end": v(-25.31, -27.34) * mm});
            skLineSegment(sketch, "E836", {"start": v(-25.31, -27.34) * mm, "end": v(-25.2, -27.4) * mm});
            skLineSegment(sketch, "E837", {"start": v(-27.24, -31.55) * mm, "end": v(-27.37, -31.48) * mm});
            skLineSegment(sketch, "E838", {"start": v(-27.37, -31.48) * mm, "end": v(-27.6, -31.93) * mm});
            skLineSegment(sketch, "E839", {"start": v(-25.2, -27.4) * mm, "end": v(-26.9, -30.6) * mm});
            skLineSegment(sketch, "E840", {"start": v(-26.9, -30.6) * mm, "end": v(-26.72, -30.7) * mm});
            skLineSegment(sketch, "E841", {"start": v(-26.72, -30.7) * mm, "end": v(-27.2, -31.58) * mm});
            skLineSegment(sketch, "E842", {"start": v(-27.2, -31.58) * mm, "end": v(-27.24, -31.55) * mm});
            skLineSegment(sketch, "E843", {"start": v(-18.85, -29.37) * mm, "end": v(-18.8, -29.25) * mm});
            skLineSegment(sketch, "E844", {"start": v(-18.8, -29.25) * mm, "end": v(-18.33, -29.43) * mm});
            skLineSegment(sketch, "E845", {"start": v(-18.33, -29.43) * mm, "end": v(-18.7, -30.36) * mm});
            skLineSegment(sketch, "E846", {"start": v(-18.7, -30.36) * mm, "end": v(-18.82, -30.31) * mm});
            skLineSegment(sketch, "E847", {"start": v(-18.82, -30.31) * mm, "end": v(-20.58, -34.86) * mm});
            skLineSegment(sketch, "E848", {"start": v(-20.58, -34.86) * mm, "end": v(-20.67, -35.1) * mm});
            skLineSegment(sketch, "E849", {"start": v(-29.1, 28.59) * mm, "end": v(-29.1, 29.09) * mm});
            skLineSegment(sketch, "E850", {"start": v(-29.1, 29.09) * mm, "end": v(-28.2, 29.09) * mm});
            skLineSegment(sketch, "E851", {"start": v(-28.2, 29.09) * mm, "end": v(-28.2, 28.59) * mm});
            skLineSegment(sketch, "E852", {"start": v(-28.2, 28.59) * mm, "end": v(-29.1, 28.59) * mm});
            skLineSegment(sketch, "E853", {"start": v(-24.5, 28.69) * mm, "end": v(-24.5, 29.09) * mm});
            skLineSegment(sketch, "E854", {"start": v(-24.5, 29.09) * mm, "end": v(-23.7, 29.09) * mm});
            skLineSegment(sketch, "E855", {"start": v(-23.7, 29.09) * mm, "end": v(-23.7, 28.69) * mm});
            skLineSegment(sketch, "E856", {"start": v(-23.7, 28.69) * mm, "end": v(-24.5, 28.69) * mm});
            skLineSegment(sketch, "E857", {"start": v(-33.63, 22.06) * mm, "end": v(-33.63, 22.46) * mm});
            skLineSegment(sketch, "E858", {"start": v(-33.63, 22.46) * mm, "end": v(-32.83, 22.46) * mm});
            skLineSegment(sketch, "E859", {"start": v(-32.83, 22.46) * mm, "end": v(-32.83, 22.06) * mm});
            skLineSegment(sketch, "E860", {"start": v(-32.83, 22.06) * mm, "end": v(-33.63, 22.06) * mm});
            skLineSegment(sketch, "E861", {"start": v(-33.63, 18.2) * mm, "end": v(-33.63, 18.6) * mm});
            skLineSegment(sketch, "E862", {"start": v(-33.63, 18.6) * mm, "end": v(-32.83, 18.6) * mm});
            skLineSegment(sketch, "E863", {"start": v(-32.83, 18.6) * mm, "end": v(-32.83, 18.2) * mm});
            skLineSegment(sketch, "E864", {"start": v(-32.83, 18.2) * mm, "end": v(-33.63, 18.2) * mm});
            skLineSegment(sketch, "E865", {"start": v(0.97, -8.77) * mm, "end": v(0.97, -9.57) * mm});
            skLineSegment(sketch, "E866", {"start": v(0.97, -9.57) * mm, "end": v(1.37, -9.57) * mm});
            skLineSegment(sketch, "E867", {"start": v(1.37, -9.57) * mm, "end": v(1.37, -8.77) * mm});
            skLineSegment(sketch, "E868", {"start": v(1.37, -8.77) * mm, "end": v(0.97, -8.77) * mm});
            skLineSegment(sketch, "E869", {"start": v(-2.68, -12) * mm, "end": v(-2.68, -12.8) * mm});
            skLineSegment(sketch, "E870", {"start": v(-2.68, -12.8) * mm, "end": v(-2.28, -12.8) * mm});
            skLineSegment(sketch, "E871", {"start": v(-2.28, -12.8) * mm, "end": v(-2.28, -12) * mm});
            skLineSegment(sketch, "E872", {"start": v(-2.28, -12) * mm, "end": v(-2.68, -12) * mm});
            skLineSegment(sketch, "E873", {"start": v(-23.84, 25.1) * mm, "end": v(-23.05, 25.22) * mm});
            skLineSegment(sketch, "E874", {"start": v(-23.05, 25.22) * mm, "end": v(-22.99, 24.83) * mm});
            skLineSegment(sketch, "E875", {"start": v(-22.99, 24.83) * mm, "end": v(-23.78, 24.7) * mm});
            skLineSegment(sketch, "E876", {"start": v(-23.78, 24.7) * mm, "end": v(-23.84, 25.1) * mm});
            skLineSegment(sketch, "E877", {"start": v(-22.4, 19.27) * mm, "end": v(-21.65, 19.54) * mm});
            skLineSegment(sketch, "E878", {"start": v(-21.65, 19.54) * mm, "end": v(-21.51, 19.16) * mm});
            skLineSegment(sketch, "E879", {"start": v(-21.51, 19.16) * mm, "end": v(-22.27, 18.9) * mm});
            skLineSegment(sketch, "E880", {"start": v(-22.27, 18.9) * mm, "end": v(-22.4, 19.27) * mm});
            skLineSegment(sketch, "E881", {"start": v(-19.95, 13.8) * mm, "end": v(-19.25, 14.2) * mm});
            skLineSegment(sketch, "E882", {"start": v(-19.25, 14.2) * mm, "end": v(-19.06, 13.85) * mm});
            skLineSegment(sketch, "E883", {"start": v(-19.06, 13.85) * mm, "end": v(-19.75, 13.45) * mm});
            skLineSegment(sketch, "E884", {"start": v(-19.75, 13.45) * mm, "end": v(-19.95, 13.8) * mm});
            skLineSegment(sketch, "E885", {"start": v(-15.95, 9.37) * mm, "end": v(-15.69, 9.06) * mm});
            skLineSegment(sketch, "E886", {"start": v(-15.69, 9.06) * mm, "end": v(-16.3, 8.55) * mm});
            skLineSegment(sketch, "E887", {"start": v(-16.3, 8.55) * mm, "end": v(-16.56, 8.85) * mm});
            skLineSegment(sketch, "E888", {"start": v(-16.56, 8.85) * mm, "end": v(-15.95, 9.37) * mm});
            skLineSegment(sketch, "E889", {"start": v(-12.38, 4.55) * mm, "end": v(-11.86, 5.16) * mm});
            skLineSegment(sketch, "E890", {"start": v(-11.86, 5.16) * mm, "end": v(-11.56, 4.9) * mm});
            skLineSegment(sketch, "E891", {"start": v(-11.56, 4.9) * mm, "end": v(-12.07, 4.3) * mm});
            skLineSegment(sketch, "E892", {"start": v(-12.07, 4.3) * mm, "end": v(-12.38, 4.55) * mm});
            skLineSegment(sketch, "E893", {"start": v(-7.46, 1.1) * mm, "end": v(-7.07, 1.8) * mm});
            skLineSegment(sketch, "E894", {"start": v(-7.07, 1.8) * mm, "end": v(-6.72, 1.6) * mm});
            skLineSegment(sketch, "E895", {"start": v(-6.72, 1.6) * mm, "end": v(-7.11, 0.9) * mm});
            skLineSegment(sketch, "E896", {"start": v(-7.11, 0.9) * mm, "end": v(-7.46, 1.1) * mm});
            skLineSegment(sketch, "E897", {"start": v(-1.73, -0.62) * mm, "end": v(-1.35, -0.76) * mm});
            skLineSegment(sketch, "E898", {"start": v(-1.35, -0.76) * mm, "end": v(-1.62, -1.51) * mm});
            skLineSegment(sketch, "E899", {"start": v(-1.62, -1.51) * mm, "end": v(-2, -1.38) * mm});
            skLineSegment(sketch, "E900", {"start": v(-2, -1.38) * mm, "end": v(-1.73, -0.62) * mm});
            skLineSegment(sketch, "E901", {"start": v(3.94, -2.1) * mm, "end": v(4.33, -2.16) * mm});
            skLineSegment(sketch, "E902", {"start": v(4.33, -2.16) * mm, "end": v(4.2, -2.95) * mm});
            skLineSegment(sketch, "E903", {"start": v(4.2, -2.95) * mm, "end": v(3.81, -2.89) * mm});
            skLineSegment(sketch, "E904", {"start": v(3.81, -2.89) * mm, "end": v(3.94, -2.1) * mm});
            skLineSegment(sketch, "E905", {"start": v(-4.4, -8.22) * mm, "end": v(-4.13, -7.46) * mm});
            skLineSegment(sketch, "E906", {"start": v(-4.13, -7.46) * mm, "end": v(-3.75, -7.6) * mm});
            skLineSegment(sketch, "E907", {"start": v(-3.75, -7.6) * mm, "end": v(-4.02, -8.35) * mm});
            skLineSegment(sketch, "E908", {"start": v(-4.02, -8.35) * mm, "end": v(-4.4, -8.22) * mm});
            skLineSegment(sketch, "E909", {"start": v(-3.54, -12.4) * mm, "end": v(-3.14, -12.46) * mm});
            skLineSegment(sketch, "E910", {"start": v(-3.14, -12.46) * mm, "end": v(-3.24, -13.25) * mm});
            skLineSegment(sketch, "E911", {"start": v(-3.24, -13.25) * mm, "end": v(-3.64, -13.2) * mm});
            skLineSegment(sketch, "E912", {"start": v(-3.64, -13.2) * mm, "end": v(-3.54, -12.4) * mm});
            skLineSegment(sketch, "E913", {"start": v(-7.24, -10.8) * mm, "end": v(-6.85, -10.9) * mm});
            skLineSegment(sketch, "E914", {"start": v(-6.85, -10.9) * mm, "end": v(-7.05, -11.68) * mm});
            skLineSegment(sketch, "E915", {"start": v(-7.05, -11.68) * mm, "end": v(-7.43, -11.58) * mm});
            skLineSegment(sketch, "E916", {"start": v(-7.43, -11.58) * mm, "end": v(-7.24, -10.8) * mm});
            skLineSegment(sketch, "E917", {"start": v(-7.45, -11.63) * mm, "end": v(-7.06, -11.72) * mm});
            skLineSegment(sketch, "E918", {"start": v(-7.06, -11.72) * mm, "end": v(-7.25, -12.5) * mm});
            skLineSegment(sketch, "E919", {"start": v(-7.25, -12.5) * mm, "end": v(-7.64, -12.4) * mm});
            skLineSegment(sketch, "E920", {"start": v(-7.64, -12.4) * mm, "end": v(-7.45, -11.63) * mm});
            skLineSegment(sketch, "E921", {"start": v(-15.24, -8.51) * mm, "end": v(-14.87, -7.8) * mm});
            skLineSegment(sketch, "E922", {"start": v(-14.87, -7.8) * mm, "end": v(-14.51, -8) * mm});
            skLineSegment(sketch, "E923", {"start": v(-14.51, -8) * mm, "end": v(-14.9, -8.7) * mm});
            skLineSegment(sketch, "E924", {"start": v(-14.9, -8.7) * mm, "end": v(-15.24, -8.51) * mm});
            skLineSegment(sketch, "E925", {"start": v(-15.27, -8.56) * mm, "end": v(-15.64, -9.26) * mm});
            skLineSegment(sketch, "E926", {"start": v(-15.64, -9.26) * mm, "end": v(-15.29, -9.45) * mm});
            skLineSegment(sketch, "E927", {"start": v(-15.29, -9.45) * mm, "end": v(-14.91, -8.75) * mm});
            skLineSegment(sketch, "E928", {"start": v(-14.91, -8.75) * mm, "end": v(-15.27, -8.56) * mm});
            skArc(sketch, "E929", {"start": v(-20.74, -14.89) * mm, "mid": v(-21, -12.41) * mm, "end": v(-21.66, -10.01) * mm});
            skArc(sketch, "E930", {"start": v(-20.46, -14.44) * mm, "mid": v(-20.8, -11.9) * mm, "end": v(-21.55, -9.44) * mm});
            skLineSegment(sketch, "E931", {"start": v(-20.74, -14.89) * mm, "end": v(-20.98, -15.3) * mm});
            skLineSegment(sketch, "E932", {"start": v(-20.98, -15.3) * mm, "end": v(-20.55, -15.54) * mm});
            skLineSegment(sketch, "E933", {"start": v(-20.55, -15.54) * mm, "end": v(-20.04, -14.68) * mm});
            skLineSegment(sketch, "E934", {"start": v(-20.04, -14.68) * mm, "end": v(-20.46, -14.44) * mm});
            skLineSegment(sketch, "E935", {"start": v(-21.55, -9.44) * mm, "end": v(-22.49, -9.8) * mm});
            skLineSegment(sketch, "E936", {"start": v(-22.49, -9.8) * mm, "end": v(-22.3, -10.26) * mm});
            skLineSegment(sketch, "E937", {"start": v(-22.3, -10.26) * mm, "end": v(-21.66, -10.01) * mm});
            skLineSegment(sketch, "E938", {"start": v(-28.84, -7.67) * mm, "end": v(-29.48, -8.3) * mm});
            skLineSegment(sketch, "E939", {"start": v(-29.48, -8.3) * mm, "end": v(-29.2, -8.59) * mm});
            skLineSegment(sketch, "E940", {"start": v(-29.2, -8.59) * mm, "end": v(-28.56, -7.95) * mm});
            skLineSegment(sketch, "E941", {"start": v(-28.56, -7.95) * mm, "end": v(-28.84, -7.67) * mm});
            skLineSegment(sketch, "E942", {"start": v(-26.93, -5.76) * mm, "end": v(-26.37, -5.2) * mm});
            skLineSegment(sketch, "E943", {"start": v(-26.37, -5.2) * mm, "end": v(-26.08, -5.48) * mm});
            skLineSegment(sketch, "E944", {"start": v(-26.08, -5.48) * mm, "end": v(-26.65, -6.04) * mm});
            skLineSegment(sketch, "E945", {"start": v(-26.65, -6.04) * mm, "end": v(-26.93, -5.76) * mm});
            skLineSegment(sketch, "E946", {"start": v(-21.28, -5.5) * mm, "end": v(-20.78, -4.87) * mm});
            skLineSegment(sketch, "E947", {"start": v(-20.78, -4.87) * mm, "end": v(-20.47, -5.12) * mm});
            skLineSegment(sketch, "E948", {"start": v(-20.47, -5.12) * mm, "end": v(-20.97, -5.74) * mm});
            skLineSegment(sketch, "E949", {"start": v(-20.97, -5.74) * mm, "end": v(-21.28, -5.5) * mm});
            skLineSegment(sketch, "E950", {"start": v(-20.75, -4.83) * mm, "end": v(-20.25, -4.2) * mm});
            skLineSegment(sketch, "E951", {"start": v(-20.25, -4.2) * mm, "end": v(-19.94, -4.46) * mm});
            skLineSegment(sketch, "E952", {"start": v(-19.94, -4.46) * mm, "end": v(-20.44, -5.08) * mm});
            skLineSegment(sketch, "E953", {"start": v(-20.44, -5.08) * mm, "end": v(-20.75, -4.83) * mm});
            skLineSegment(sketch, "E954", {"start": v(-26.63, -0.08) * mm, "end": v(-26.01, 0.42) * mm});
            skLineSegment(sketch, "E955", {"start": v(-26.01, 0.42) * mm, "end": v(-25.76, 0.1) * mm});
            skLineSegment(sketch, "E956", {"start": v(-25.76, 0.1) * mm, "end": v(-26.38, -0.4) * mm});
            skLineSegment(sketch, "E957", {"start": v(-26.38, -0.4) * mm, "end": v(-26.63, -0.08) * mm});
            skLineSegment(sketch, "E958", {"start": v(-25.97, 0.45) * mm, "end": v(-25.35, 0.95) * mm});
            skLineSegment(sketch, "E959", {"start": v(-25.35, 0.95) * mm, "end": v(-25.1, 0.64) * mm});
            skLineSegment(sketch, "E960", {"start": v(-25.1, 0.64) * mm, "end": v(-25.72, 0.14) * mm});
            skLineSegment(sketch, "E961", {"start": v(-25.72, 0.14) * mm, "end": v(-25.97, 0.45) * mm});
            skArc(sketch, "E962", {"start": v(-30.9, -0.77) * mm, "mid": v(-33.3, -0.11) * mm, "end": v(-35.78, 0.15) * mm});
            skArc(sketch, "E963", {"start": v(-30.33, -0.66) * mm, "mid": v(-32.78, 0.09) * mm, "end": v(-35.33, 0.43) * mm});
            skLineSegment(sketch, "E964", {"start": v(-30.9, -0.77) * mm, "end": v(-31.15, -1.42) * mm});
            skLineSegment(sketch, "E965", {"start": v(-31.15, -1.42) * mm, "end": v(-30.69, -1.6) * mm});
            skLineSegment(sketch, "E966", {"start": v(-30.69, -1.6) * mm, "end": v(-30.33, -0.66) * mm});
            skLineSegment(sketch, "E967", {"start": v(-35.33, 0.43) * mm, "end": v(-35.57, 0.85) * mm});
            skLineSegment(sketch, "E968", {"start": v(-35.57, 0.85) * mm, "end": v(-36.44, 0.35) * mm});
            skLineSegment(sketch, "E969", {"start": v(-36.44, 0.35) * mm, "end": v(-36.18, -0.09) * mm});
            skLineSegment(sketch, "E970", {"start": v(-36.18, -0.09) * mm, "end": v(-35.78, 0.15) * mm});
            skLineSegment(sketch, "E971", {"start": v(-30.16, 5.25) * mm, "end": v(-29.45, 5.62) * mm});
            skLineSegment(sketch, "E972", {"start": v(-29.45, 5.62) * mm, "end": v(-29.64, 5.98) * mm});
            skLineSegment(sketch, "E973", {"start": v(-29.64, 5.98) * mm, "end": v(-30.34, 5.6) * mm});
            skLineSegment(sketch, "E974", {"start": v(-30.34, 5.6) * mm, "end": v(-30.16, 5.25) * mm});
            skLineSegment(sketch, "E975", {"start": v(-29.6, 6) * mm, "end": v(-28.89, 6.38) * mm});
            skLineSegment(sketch, "E976", {"start": v(-28.89, 6.38) * mm, "end": v(-28.7, 6.02) * mm});
            skLineSegment(sketch, "E977", {"start": v(-28.7, 6.02) * mm, "end": v(-29.4, 5.65) * mm});
            skLineSegment(sketch, "E978", {"start": v(-29.4, 5.65) * mm, "end": v(-29.6, 6) * mm});
            skLineSegment(sketch, "E979", {"start": v(-39.47, 6.74) * mm, "end": v(-38.54, 7.1) * mm});
            skLineSegment(sketch, "E980", {"start": v(-38.54, 7.1) * mm, "end": v(-38.36, 6.63) * mm});
            skLineSegment(sketch, "E981", {"start": v(-38.36, 6.63) * mm, "end": v(-39.3, 6.27) * mm});
            skLineSegment(sketch, "E982", {"start": v(-39.3, 6.27) * mm, "end": v(-39.47, 6.74) * mm});
            skLineSegment(sketch, "E983", {"start": v(-41.04, 11.75) * mm, "end": v(-40.07, 12) * mm});
            skLineSegment(sketch, "E984", {"start": v(-40.07, 12) * mm, "end": v(-39.95, 11.52) * mm});
            skLineSegment(sketch, "E985", {"start": v(-39.95, 11.52) * mm, "end": v(-40.92, 11.27) * mm});
            skLineSegment(sketch, "E986", {"start": v(-40.92, 11.27) * mm, "end": v(-41.04, 11.75) * mm});
            skLineSegment(sketch, "E987", {"start": v(-41.95, 16.65) * mm, "end": v(-41.89, 16.15) * mm});
            skLineSegment(sketch, "E988", {"start": v(-41.89, 16.15) * mm, "end": v(-40.9, 16.28) * mm});
            skLineSegment(sketch, "E989", {"start": v(-40.9, 16.28) * mm, "end": v(-40.96, 16.78) * mm});
            skLineSegment(sketch, "E990", {"start": v(-40.96, 16.78) * mm, "end": v(-41.95, 16.65) * mm});
            skLineSegment(sketch, "E991", {"start": v(-33.3, 13.25) * mm, "end": v(-32.52, 13.45) * mm});
            skLineSegment(sketch, "E992", {"start": v(-32.52, 13.45) * mm, "end": v(-32.62, 13.83) * mm});
            skLineSegment(sketch, "E993", {"start": v(-32.62, 13.83) * mm, "end": v(-33.4, 13.64) * mm});
            skLineSegment(sketch, "E994", {"start": v(-33.4, 13.64) * mm, "end": v(-33.3, 13.25) * mm});
            skLineSegment(sketch, "E995", {"start": v(-32.57, 13.85) * mm, "end": v(-32.47, 13.46) * mm});
            skLineSegment(sketch, "E996", {"start": v(-32.47, 13.46) * mm, "end": v(-31.7, 13.65) * mm});
            skLineSegment(sketch, "E997", {"start": v(-31.7, 13.65) * mm, "end": v(-31.8, 14.04) * mm});
            skLineSegment(sketch, "E998", {"start": v(-31.8, 14.04) * mm, "end": v(-32.57, 13.85) * mm});
            skLineSegment(sketch, "E999", {"start": v(-34.14, 17.65) * mm, "end": v(-34.1, 17.25) * mm});
            skLineSegment(sketch, "E1000", {"start": v(-34.1, 17.25) * mm, "end": v(-33.3, 17.35) * mm});
            skLineSegment(sketch, "E1001", {"start": v(-33.3, 17.35) * mm, "end": v(-33.35, 17.75) * mm});
            skLineSegment(sketch, "E1002", {"start": v(-33.35, 17.75) * mm, "end": v(-34.14, 17.65) * mm});
            skLineSegment(sketch, "E1003", {"start": v(-29.1, 16.5) * mm, "end": v(-28.35, 16.76) * mm});
            skLineSegment(sketch, "E1004", {"start": v(-28.35, 16.76) * mm, "end": v(-28.49, 17.14) * mm});
            skLineSegment(sketch, "E1005", {"start": v(-28.49, 17.14) * mm, "end": v(-29.24, 16.87) * mm});
            skLineSegment(sketch, "E1006", {"start": v(-29.24, 16.87) * mm, "end": v(-29.1, 16.5) * mm});
            skLineSegment(sketch, "E1007", {"start": v(-30.4, 22.1) * mm, "end": v(-29.6, 22.1) * mm});
            skLineSegment(sketch, "E1008", {"start": v(-29.6, 22.1) * mm, "end": v(-29.6, 22.1) * mm});
            skLineSegment(sketch, "E1009", {"start": v(-29.6, 22.1) * mm, "end": v(-29.6, 21.7) * mm});
            skLineSegment(sketch, "E1010", {"start": v(-29.6, 21.7) * mm, "end": v(-30.4, 21.7) * mm});
            skLineSegment(sketch, "E1011", {"start": v(-30.4, 21.7) * mm, "end": v(-30.4, 22.1) * mm});
            skLineSegment(sketch, "E1012", {"start": v(-42.18, 22.46) * mm, "end": v(-42.18, 21.96) * mm});
            skLineSegment(sketch, "E1013", {"start": v(-42.18, 21.96) * mm, "end": v(-41.56, 21.96) * mm});
            skLineSegment(sketch, "E1014", {"start": v(-41.4, 18.6) * mm, "end": v(-42.03, 18.6) * mm});
            skLineSegment(sketch, "E1015", {"start": v(-42.03, 18.6) * mm, "end": v(-42.03, 18.2) * mm});
            skLineSegment(sketch, "E1016", {"start": v(-42.03, 18.2) * mm, "end": v(-41.37, 18.2) * mm});
            skLineSegment(sketch, "E1017", {"start": v(-41.37, 18.2) * mm, "end": v(-41.28, 17.29) * mm});
            skLineSegment(sketch, "E1018", {"start": v(-41.28, 17.29) * mm, "end": v(-42.02, 17.2) * mm});
            skLineSegment(sketch, "E1019", {"start": v(-42.02, 17.2) * mm, "end": v(-41.96, 16.7) * mm});
            skLineSegment(sketch, "E1020", {"start": v(-41.96, 16.7) * mm, "end": v(-40.97, 16.83) * mm});
            skLineSegment(sketch, "E1021", {"start": v(-40.97, 16.83) * mm, "end": v(-41.02, 17.25) * mm});
            skLineSegment(sketch, "E1022", {"start": v(-41.02, 17.25) * mm, "end": v(-40.58, 17.3) * mm});
            skLineSegment(sketch, "E1023", {"start": v(-40.58, 17.3) * mm, "end": v(-40.67, 18.2) * mm});
            skLineSegment(sketch, "E1024", {"start": v(-40.67, 18.2) * mm, "end": v(-33.68, 18.2) * mm});
            skLineSegment(sketch, "E1025", {"start": v(-33.68, 18.2) * mm, "end": v(-33.68, 22.46) * mm});
            skLineSegment(sketch, "E1026", {"start": v(-33.68, 22.46) * mm, "end": v(-34.58, 22.46) * mm});
            skLineSegment(sketch, "E1027", {"start": v(-34.58, 22.46) * mm, "end": v(-34.58, 22.2) * mm});
            skLineSegment(sketch, "E1028", {"start": v(-34.58, 22.2) * mm, "end": v(-41.28, 22.2) * mm});
            skLineSegment(sketch, "E1029", {"start": v(-41.28, 22.2) * mm, "end": v(-41.28, 22.46) * mm});
            skLineSegment(sketch, "E1030", {"start": v(-41.28, 22.46) * mm, "end": v(-42.18, 22.46) * mm});
            skArc(sketch, "E1031", {"start": v(-41.56, 21.96) * mm, "mid": v(-41.51, 20.28) * mm, "end": v(-41.4, 18.6) * mm});
            skLineSegment(sketch, "E1032", {"start": v(-26.25, 10.22) * mm, "end": v(-25.56, 10.61) * mm});
            skLineSegment(sketch, "E1033", {"start": v(-25.56, 10.61) * mm, "end": v(-25.36, 10.27) * mm});
            skLineSegment(sketch, "E1034", {"start": v(-25.36, 10.27) * mm, "end": v(-26.05, 9.87) * mm});
            skLineSegment(sketch, "E1035", {"start": v(-26.05, 9.87) * mm, "end": v(-26.25, 10.22) * mm});
            skLineSegment(sketch, "E1036", {"start": v(-22.12, 4.2) * mm, "end": v(-21.51, 4.72) * mm});
            skLineSegment(sketch, "E1037", {"start": v(-21.51, 4.72) * mm, "end": v(-21.25, 4.41) * mm});
            skLineSegment(sketch, "E1038", {"start": v(-21.25, 4.41) * mm, "end": v(-21.87, 3.9) * mm});
            skLineSegment(sketch, "E1039", {"start": v(-21.87, 3.9) * mm, "end": v(-22.12, 4.2) * mm});
            skLineSegment(sketch, "E1040", {"start": v(-17, -0.98) * mm, "end": v(-16.48, -0.37) * mm});
            skLineSegment(sketch, "E1041", {"start": v(-16.48, -0.37) * mm, "end": v(-16.17, -0.62) * mm});
            skLineSegment(sketch, "E1042", {"start": v(-16.17, -0.62) * mm, "end": v(-16.68, -1.23) * mm});
            skLineSegment(sketch, "E1043", {"start": v(-16.68, -1.23) * mm, "end": v(-17, -0.98) * mm});
            skLineSegment(sketch, "E1044", {"start": v(-10.62, -4.47) * mm, "end": v(-10.28, -4.67) * mm});
            skLineSegment(sketch, "E1045", {"start": v(-10.28, -4.67) * mm, "end": v(-10.67, -5.36) * mm});
            skLineSegment(sketch, "E1046", {"start": v(-10.67, -5.36) * mm, "end": v(-11.02, -5.16) * mm});
            skLineSegment(sketch, "E1047", {"start": v(-11.02, -5.16) * mm, "end": v(-10.62, -4.47) * mm});
            skLineSegment(sketch, "E1048", {"start": v(-14.26, -17.47) * mm, "end": v(-13.8, -17.65) * mm});
            skLineSegment(sketch, "E1049", {"start": v(-13.8, -17.65) * mm, "end": v(-14.15, -18.58) * mm});
            skLineSegment(sketch, "E1050", {"start": v(-14.15, -18.58) * mm, "end": v(-14.62, -18.4) * mm});
            skLineSegment(sketch, "E1051", {"start": v(-14.62, -18.4) * mm, "end": v(-14.26, -17.47) * mm});
            skLineSegment(sketch, "E1052", {"start": v(-9.62, -20.02) * mm, "end": v(-9.38, -19.06) * mm});
            skLineSegment(sketch, "E1053", {"start": v(-9.38, -19.06) * mm, "end": v(-8.9, -19.18) * mm});
            skLineSegment(sketch, "E1054", {"start": v(-8.9, -19.18) * mm, "end": v(-9.14, -20.15) * mm});
            skLineSegment(sketch, "E1055", {"start": v(-9.14, -20.15) * mm, "end": v(-9.62, -20.02) * mm});
            skArc(sketch, "E1056", {"start": v(-12.9, -13.97) * mm, "mid": v(-8.35, -15.45) * mm, "end": v(-3.64, -16.35) * mm});
            skArc(sketch, "E1057", {"start": v(-14.2, -17.33) * mm, "mid": v(-9.23, -18.94) * mm, "end": v(-4.1, -19.92) * mm});
            skLineSegment(sketch, "E1058", {"start": v(-12.9, -13.97) * mm, "end": v(-14.2, -17.33) * mm});
            skLineSegment(sketch, "E1059", {"start": v(-3.64, -16.35) * mm, "end": v(-4.1, -19.92) * mm});
            skLineSegment(sketch, "E1060", {"start": v(-4.07, -20.08) * mm, "end": v(-4.2, -21.07) * mm});
            skLineSegment(sketch, "E1061", {"start": v(-4.2, -21.07) * mm, "end": v(-3.7, -21.13) * mm});
            skLineSegment(sketch, "E1062", {"start": v(-3.7, -21.13) * mm, "end": v(-3.6, -20.39) * mm});
            skLineSegment(sketch, "E1063", {"start": v(-3.6, -20.39) * mm, "end": v(-2.68, -20.48) * mm});
            skLineSegment(sketch, "E1064", {"start": v(-2.68, -20.48) * mm, "end": v(-2.68, -21.14) * mm});
            skLineSegment(sketch, "E1065", {"start": v(-2.68, -21.14) * mm, "end": v(-2.28, -21.14) * mm});
            skLineSegment(sketch, "E1066", {"start": v(-2.28, -21.14) * mm, "end": v(-2.29, -20.52) * mm});
            skLineSegment(sketch, "E1067", {"start": v(-4.07, -20.08) * mm, "end": v(-3.64, -20.13) * mm});
            skLineSegment(sketch, "E1068", {"start": v(-3.64, -20.13) * mm, "end": v(-3.58, -19.68) * mm});
            skLineSegment(sketch, "E1069", {"start": v(-3.58, -19.68) * mm, "end": v(-2.68, -19.78) * mm});
            skLineSegment(sketch, "E1070", {"start": v(-2.68, -19.78) * mm, "end": v(-2.68, -12.84) * mm});
            skLineSegment(sketch, "E1071", {"start": v(-2.68, -12.84) * mm, "end": v(-0.25, -12.84) * mm});
            skLineSegment(sketch, "E1072", {"start": v(-0.25, -12.84) * mm, "end": v(-0.25, -12) * mm});
            skLineSegment(sketch, "E1073", {"start": v(-0.25, -12) * mm, "end": v(1.47, -12) * mm});
            skLineSegment(sketch, "E1074", {"start": v(1.47, -12) * mm, "end": v(1.47, -12.84) * mm});
            skLineSegment(sketch, "E1075", {"start": v(1.47, -12.84) * mm, "end": v(1.57, -12.84) * mm});
            skLineSegment(sketch, "E1076", {"start": v(1.57, -12.84) * mm, "end": v(1.57, -13.74) * mm});
            skLineSegment(sketch, "E1077", {"start": v(1.57, -13.74) * mm, "end": v(1.32, -13.74) * mm});
            skLineSegment(sketch, "E1078", {"start": v(1.32, -13.74) * mm, "end": v(1.32, -20.44) * mm});
            skLineSegment(sketch, "E1079", {"start": v(1.32, -20.44) * mm, "end": v(1.57, -20.44) * mm});
            skLineSegment(sketch, "E1080", {"start": v(1.57, -20.44) * mm, "end": v(1.57, -21.44) * mm});
            skLineSegment(sketch, "E1081", {"start": v(1.57, -21.44) * mm, "end": v(1.07, -21.44) * mm});
            skLineSegment(sketch, "E1082", {"start": v(1.07, -21.44) * mm, "end": v(1.07, -20.67) * mm});
            skArc(sketch, "E1083", {"start": v(-2.28, -20.52) * mm, "mid": v(-0.6, -20.62) * mm, "end": v(1.07, -20.67) * mm});
            skLineSegment(sketch, "E1084", {"start": v(56.24, -27.44) * mm, "end": v(56.24, -28.42) * mm});
            skLineSegment(sketch, "E1085", {"start": v(56.24, -28.42) * mm, "end": v(56, -28.42) * mm});
            skLineSegment(sketch, "E1086", {"start": v(56, -28.42) * mm, "end": v(56, -29.26) * mm});
            skLineSegment(sketch, "E1087", {"start": v(56, -29.26) * mm, "end": v(56.6, -29.26) * mm});
            skLineSegment(sketch, "E1088", {"start": v(56.6, -29.26) * mm, "end": v(56.6, -30.47) * mm});
            skLineSegment(sketch, "E1089", {"start": v(56.6, -30.47) * mm, "end": v(56.74, -30.47) * mm});
            skLineSegment(sketch, "E1090", {"start": v(56.74, -30.47) * mm, "end": v(56.74, -31.37) * mm});
            skLineSegment(sketch, "E1091", {"start": v(56.74, -31.37) * mm, "end": v(56.6, -31.37) * mm});
            skLineSegment(sketch, "E1092", {"start": v(56.6, -31.37) * mm, "end": v(56.6, -31.73) * mm});
            skLineSegment(sketch, "E1093", {"start": v(56.6, -31.73) * mm, "end": v(56.74, -31.73) * mm});
            skLineSegment(sketch, "E1094", {"start": v(56.74, -31.73) * mm, "end": v(56.74, -32.63) * mm});
            skLineSegment(sketch, "E1095", {"start": v(56.74, -32.63) * mm, "end": v(56.6, -32.63) * mm});
            skLineSegment(sketch, "E1096", {"start": v(56.6, -32.63) * mm, "end": v(56.6, -33.3) * mm});
            skLineSegment(sketch, "E1097", {"start": v(56.6, -33.3) * mm, "end": v(56.24, -33.3) * mm});
            skLineSegment(sketch, "E1098", {"start": v(56.24, -33.3) * mm, "end": v(56.24, -34.4) * mm});
            skLineSegment(sketch, "E1099", {"start": v(56.24, -34.4) * mm, "end": v(56.84, -34.4) * mm});
            skLineSegment(sketch, "E1100", {"start": v(56.84, -34.4) * mm, "end": v(56.84, -34) * mm});
            skLineSegment(sketch, "E1101", {"start": v(56.84, -34) * mm, "end": v(59.17, -34) * mm});
            skLineSegment(sketch, "E1102", {"start": v(59.17, -34) * mm, "end": v(59.17, -28.1) * mm});
            skLineSegment(sketch, "E1103", {"start": v(59.17, -28.1) * mm, "end": v(56.84, -28.1) * mm});
            skLineSegment(sketch, "E1104", {"start": v(56.84, -28.1) * mm, "end": v(56.84, -27.44) * mm});
            skLineSegment(sketch, "E1105", {"start": v(56.84, -27.44) * mm, "end": v(56.24, -27.44) * mm});
            skLineSegment(sketch, "E1106", {"start": v(45.7, 25.33) * mm, "end": v(45.7, 24.53) * mm});
            skLineSegment(sketch, "E1107", {"start": v(45.7, 24.53) * mm, "end": v(46.5, 24.53) * mm});
            skLineSegment(sketch, "E1108", {"start": v(46.5, 24.53) * mm, "end": v(46.5, 25.33) * mm});
            skLineSegment(sketch, "E1109", {"start": v(46.5, 25.33) * mm, "end": v(45.7, 25.33) * mm});
            skLineSegment(sketch, "E1110", {"start": v(42.83, 35.8) * mm, "end": v(42.83, 29.46) * mm});
            skLineSegment(sketch, "E1111", {"start": v(42.83, 29.46) * mm, "end": v(45.7, 29.46) * mm});
            skLineSegment(sketch, "E1112", {"start": v(45.7, 29.46) * mm, "end": v(45.7, 28.9) * mm});
            skLineSegment(sketch, "E1113", {"start": v(45.7, 28.9) * mm, "end": v(46.5, 28.9) * mm});
            skLineSegment(sketch, "E1114", {"start": v(46.5, 28.9) * mm, "end": v(46.5, 29.46) * mm});
            skLineSegment(sketch, "E1115", {"start": v(46.5, 29.46) * mm, "end": v(53.7, 29.46) * mm});
            skLineSegment(sketch, "E1116", {"start": v(53.7, 29.46) * mm, "end": v(53.7, 28.9) * mm});
            skLineSegment(sketch, "E1117", {"start": v(53.7, 28.9) * mm, "end": v(54.5, 28.9) * mm});
            skLineSegment(sketch, "E1118", {"start": v(54.5, 28.9) * mm, "end": v(54.5, 29.44) * mm});
            skArc(sketch, "E1119", {"start": v(58.56, 25.33) * mm, "mid": v(57.28, 28.14) * mm, "end": v(54.5, 29.44) * mm});
            skLineSegment(sketch, "E1120", {"start": v(58.56, 25.33) * mm, "end": v(58.22, 25.33) * mm});
            skLineSegment(sketch, "E1121", {"start": v(58.22, 25.33) * mm, "end": v(58.22, 24.33) * mm});
            skLineSegment(sketch, "E1122", {"start": v(58.22, 24.33) * mm, "end": v(58.57, 24.33) * mm});
            skLineSegment(sketch, "E1123", {"start": v(58.57, 24.33) * mm, "end": v(58.57, 20.4) * mm});
            skLineSegment(sketch, "E1124", {"start": v(58.57, 20.4) * mm, "end": v(58.22, 20.4) * mm});
            skLineSegment(sketch, "E1125", {"start": v(58.22, 20.4) * mm, "end": v(58.22, 19.4) * mm});
            skLineSegment(sketch, "E1126", {"start": v(58.22, 19.4) * mm, "end": v(58.82, 19.4) * mm});
            skLineSegment(sketch, "E1127", {"start": v(58.82, 19.4) * mm, "end": v(58.82, 25.15) * mm});
            skArc(sketch, "E1128", {"start": v(58.82, 25.15) * mm, "mid": v(57.39, 28.38) * mm, "end": v(54.12, 29.7) * mm});
            skLineSegment(sketch, "E1129", {"start": v(54.12, 29.7) * mm, "end": v(43.08, 29.7) * mm});
            skLineSegment(sketch, "E1130", {"start": v(43.08, 29.7) * mm, "end": v(43.08, 35.56) * mm});
            skLineSegment(sketch, "E1131", {"start": v(43.08, 35.56) * mm, "end": v(54.92, 35.53) * mm});
            skArc(sketch, "E1132", {"start": v(64.66, 25.33) * mm, "mid": v(61.74, 32.3) * mm, "end": v(54.92, 35.53) * mm});
            skLineSegment(sketch, "E1133", {"start": v(64.66, 25.33) * mm, "end": v(64.37, 25.33) * mm});
            skLineSegment(sketch, "E1134", {"start": v(64.37, 25.33) * mm, "end": v(64.37, 24.53) * mm});
            skLineSegment(sketch, "E1135", {"start": v(64.37, 24.53) * mm, "end": v(64.67, 24.53) * mm});
            skLineSegment(sketch, "E1136", {"start": v(64.67, 24.53) * mm, "end": v(64.67, 20.2) * mm});
            skLineSegment(sketch, "E1137", {"start": v(64.67, 20.2) * mm, "end": v(64.37, 20.2) * mm});
            skLineSegment(sketch, "E1138", {"start": v(64.37, 20.2) * mm, "end": v(64.37, 19.4) * mm});
            skLineSegment(sketch, "E1139", {"start": v(64.37, 19.4) * mm, "end": v(65.17, 19.4) * mm});
            skLineSegment(sketch, "E1140", {"start": v(65.17, 19.4) * mm, "end": v(65.17, 20.2) * mm});
            skLineSegment(sketch, "E1141", {"start": v(65.17, 20.2) * mm, "end": v(64.92, 20.2) * mm});
            skLineSegment(sketch, "E1142", {"start": v(64.92, 20.2) * mm, "end": v(64.92, 24.53) * mm});
            skLineSegment(sketch, "E1143", {"start": v(64.92, 24.53) * mm, "end": v(65.17, 24.53) * mm});
            skLineSegment(sketch, "E1144", {"start": v(65.17, 24.53) * mm, "end": v(65.17, 25.33) * mm});
            skLineSegment(sketch, "E1145", {"start": v(65.17, 25.33) * mm, "end": v(64.91, 25.33) * mm});
            skArc(sketch, "E1146", {"start": v(64.91, 25.33) * mm, "mid": v(64.1, 29.14) * mm, "end": v(61.99, 32.4) * mm});
            skLineSegment(sketch, "E1147", {"start": v(61.99, 32.4) * mm, "end": v(62.23, 32.66) * mm});
            skLineSegment(sketch, "E1148", {"start": v(62.23, 32.66) * mm, "end": v(61.51, 33.35) * mm});
            skLineSegment(sketch, "E1149", {"start": v(61.51, 33.35) * mm, "end": v(61.27, 33.1) * mm});
            skArc(sketch, "E1150", {"start": v(61.27, 33.1) * mm, "mid": v(58.11, 35.04) * mm, "end": v(54.5, 35.8) * mm});
            skLineSegment(sketch, "E1151", {"start": v(54.5, 35.8) * mm, "end": v(54.5, 36.36) * mm});
            skLineSegment(sketch, "E1152", {"start": v(54.5, 36.36) * mm, "end": v(53.7, 36.36) * mm});
            skLineSegment(sketch, "E1153", {"start": v(53.7, 36.36) * mm, "end": v(53.7, 35.8) * mm});
            skLineSegment(sketch, "E1154", {"start": v(53.7, 35.8) * mm, "end": v(46.5, 35.8) * mm});
            skLineSegment(sketch, "E1155", {"start": v(46.5, 35.8) * mm, "end": v(46.5, 36.36) * mm});
            skLineSegment(sketch, "E1156", {"start": v(46.5, 36.36) * mm, "end": v(45.7, 36.36) * mm});
            skLineSegment(sketch, "E1157", {"start": v(45.7, 36.36) * mm, "end": v(45.7, 35.8) * mm});
            skLineSegment(sketch, "E1158", {"start": v(45.7, 35.8) * mm, "end": v(42.83, 35.8) * mm});
            skSolve(sketch);
        }
        {
            var Q0;
            Q0=makeQuery(id+"F0.imprint","IMPRINT",FACE,{"disambiguationData":[TD([[makeQuery(id+"F0.imprint","IMPRINT",EDGE,{"derivedFrom":sQuery(id+"F0.wireOp",EDGE,"E0")}),-1.0]])]});
            extrude(context, id + "F1", {"entities" : qUnion([Q0]), "depth" : 25 * mm});
        }
    });
